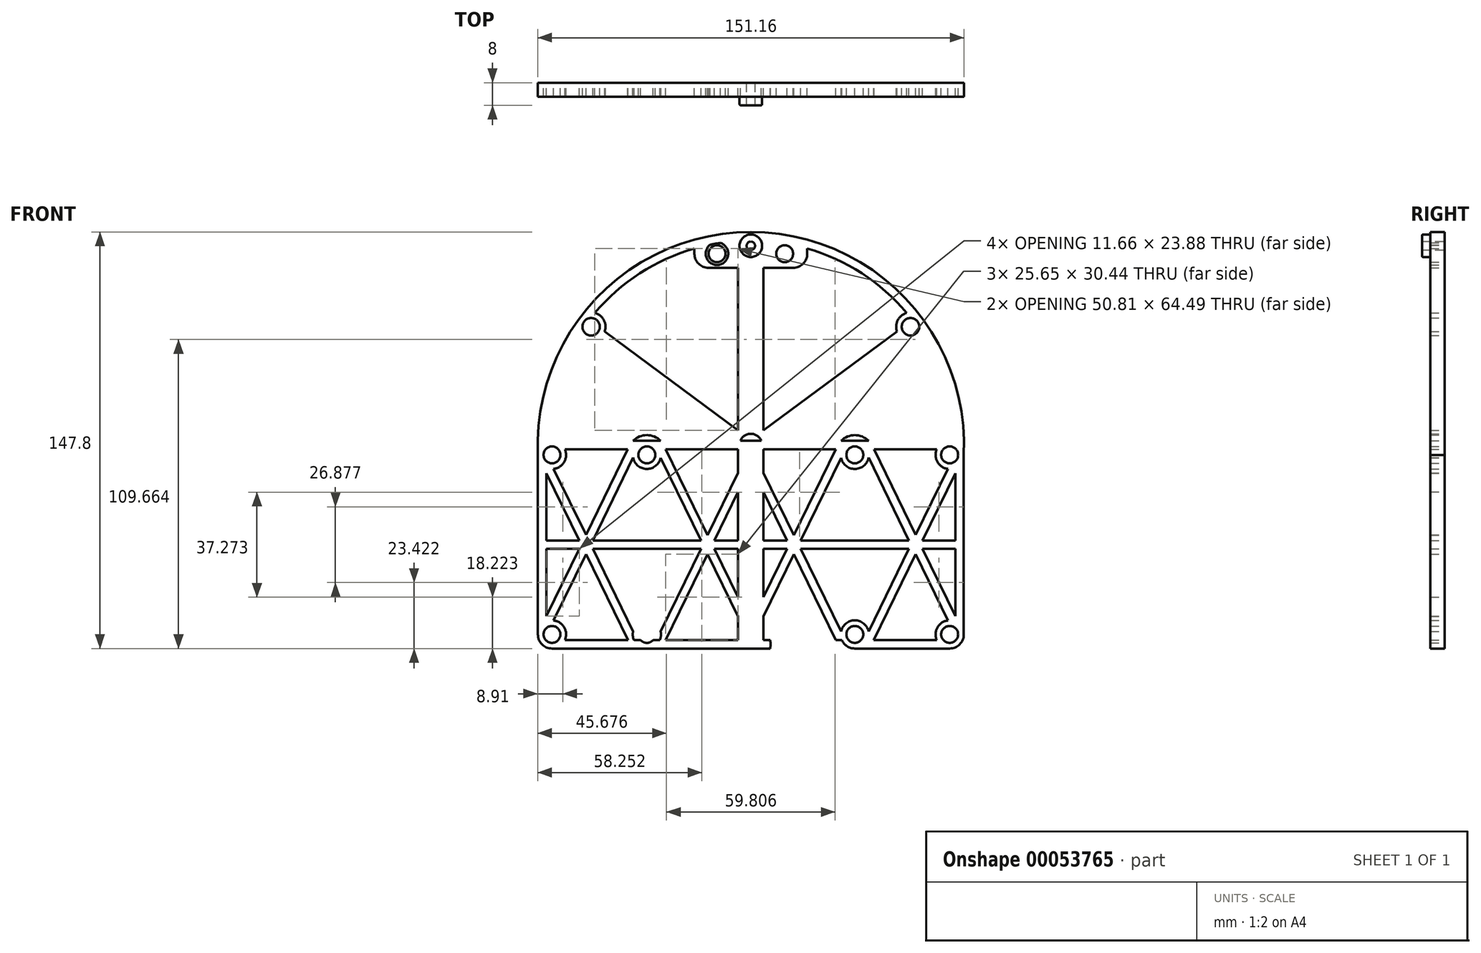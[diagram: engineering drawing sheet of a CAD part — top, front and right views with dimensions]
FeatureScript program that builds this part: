
annotation { "Feature Type Name" : "Feature", "Feature Type Description" : "" }
export const myFeature = defineFeature(function(context is Context, id is Id, definition is map)
    precondition{}
    {
        {
            var Q0;
            Q0=qCreatedBy(makeId("Front.planeOp"),FACE);
            var sketch = newSketch(context, id + "F0", { "sketchPlane" : qUnion([Q0])});
            skPoint(sketch, "E0", {"position": v(-3.58, 32.7) * mm});
            skPoint(sketch, "E1", {"position": v(-3.58, -38) * mm});
            skLineSegment(sketch, "E2.bottom", {"start": v(-8.08, 122.7) * mm, "end": v(0.92, 122.7) * mm});
            skLineSegment(sketch, "E2.top", {"start": v(-8.08, -57.3) * mm, "end": v(0.92, -57.3) * mm});
            skLineSegment(sketch, "E2.left", {"start": v(-8.08, 122.7) * mm, "end": v(-8.08, -57.3) * mm});
            skLineSegment(sketch, "E2.right", {"start": v(0.92, 122.7) * mm, "end": v(0.92, -57.3) * mm});
            skLineSegment(sketch, "E3", {"start": v(-3.58, 122.7) * mm, "end": v(-3.58, -57.3) * mm, "construction": true});
            skCircle(sketch, "E4", {"center": v(-3.58, 32.7) * mm, "radius": 1.5 * mm});
            skCircle(sketch, "E5", {"center": v(-3.58, -38) * mm, "radius": 1.5 * mm});
            skCircle(sketch, "E6", {"center": v(-3.58, 32.7) * mm, "radius": 4 * mm});
            skCircle(sketch, "E7", {"center": v(-3.58, -38) * mm, "radius": 4 * mm});
            skCircle(sketch, "E8", {"center": v(-3.58, 103.42) * mm, "radius": 1.5 * mm});
            skCircle(sketch, "E9", {"center": v(-3.58, 103.42) * mm, "radius": 4 * mm});
            skLineSegment(sketch, "E10.bottom", {"start": v(-76.08, -36.5) * mm, "end": v(68.92, -36.5) * mm});
            skLineSegment(sketch, "E10.top", {"start": v(-76.08, -39.5) * mm, "end": v(68.92, -39.5) * mm});
            skLineSegment(sketch, "E10.left", {"start": v(-76.08, -36.5) * mm, "end": v(-76.08, -39.5) * mm});
            skLineSegment(sketch, "E10.right", {"start": v(68.92, -36.5) * mm, "end": v(68.92, -39.5) * mm});
            skPoint(sketch, "E11", {"position": v(-3.58, -36.5) * mm});
            skPoint(sketch, "E12", {"position": v(-3.58, 34.2) * mm});
            skLineSegment(sketch, "E13.bottom", {"start": v(-76.08, 34.2) * mm, "end": v(68.92, 34.2) * mm});
            skLineSegment(sketch, "E13.top", {"start": v(-76.08, 31.2) * mm, "end": v(68.92, 31.2) * mm});
            skLineSegment(sketch, "E13.right", {"start": v(68.92, 34.2) * mm, "end": v(68.92, 31.2) * mm});
            skLineSegment(sketch, "E13.left", {"start": v(-76.08, 34.2) * mm, "end": v(-76.08, 31.2) * mm});
            skLineSegment(sketch, "E14.bottom", {"start": v(68.92, 34.2) * mm, "end": v(71.92, 34.2) * mm});
            skLineSegment(sketch, "E14.top", {"start": v(68.92, -39.5) * mm, "end": v(71.92, -39.5) * mm});
            skLineSegment(sketch, "E14.left", {"start": v(68.92, 34.2) * mm, "end": v(68.92, -39.5) * mm});
            skLineSegment(sketch, "E14.right", {"start": v(71.92, 34.2) * mm, "end": v(71.92, -39.5) * mm});
            skLineSegment(sketch, "E15.bottom", {"start": v(-76.08, 34.2) * mm, "end": v(-79.08, 34.2) * mm});
            skLineSegment(sketch, "E15.top", {"start": v(-76.08, -39.5) * mm, "end": v(-79.08, -39.5) * mm});
            skLineSegment(sketch, "E15.left", {"start": v(-76.08, 34.2) * mm, "end": v(-76.08, -39.5) * mm});
            skLineSegment(sketch, "E15.right", {"start": v(-79.08, 34.2) * mm, "end": v(-79.08, -39.5) * mm});
            skLineSegment(sketch, "E16", {"start": v(66.92, 34.2) * mm, "end": v(66.92, 29.2) * mm, "construction": true});
            skLineSegment(sketch, "E17", {"start": v(66.92, -39.5) * mm, "end": v(66.92, -34.5) * mm, "construction": true});
            skLineSegment(sketch, "E18", {"start": v(-74.08, 34.2) * mm, "end": v(-74.08, 29.2) * mm, "construction": true});
            skLineSegment(sketch, "E19", {"start": v(-74.08, -39.5) * mm, "end": v(-74.08, -34.5) * mm, "construction": true});
            skCircle(sketch, "E20", {"center": v(-3.58, -38) * mm, "radius": 64 * mm, "construction": true});
            skCircle(sketch, "E21", {"center": v(-3.58, 32.7) * mm, "radius": 64 * mm, "construction": true});
            skCircle(sketch, "E22", {"center": v(66.92, 29.2) * mm, "radius": 5 * mm});
            skCircle(sketch, "E23", {"center": v(66.92, -34.5) * mm, "radius": 5 * mm});
            skCircle(sketch, "E24", {"center": v(-74.08, -34.5) * mm, "radius": 5 * mm});
            skCircle(sketch, "E25", {"center": v(-74.08, 29.2) * mm, "radius": 5 * mm});
            skCircle(sketch, "E26", {"center": v(66.92, -34.5) * mm, "radius": 3 * mm});
            skCircle(sketch, "E27", {"center": v(66.92, 29.2) * mm, "radius": 3 * mm});
            skCircle(sketch, "E28", {"center": v(-74.08, 29.2) * mm, "radius": 3 * mm});
            skCircle(sketch, "E29", {"center": v(-74.08, -34.5) * mm, "radius": 3 * mm});
            skLineSegment(sketch, "E30", {"start": v(33.28, 34.2) * mm, "end": v(33.28, 29.2) * mm, "construction": true});
            skCircle(sketch, "E31", {"center": v(33.28, 29.2) * mm, "radius": 5 * mm});
            skCircle(sketch, "E32", {"center": v(33.28, 29.2) * mm, "radius": 3 * mm});
            skCircle(sketch, "E33.0.1.0", {"center": v(33.28, -34.5) * mm, "radius": 3 * mm});
            skCircle(sketch, "E33.0.1.1", {"center": v(33.28, -34.5) * mm, "radius": 5 * mm});
            skCircle(sketch, "E33.1.0.0", {"center": v(-40.44, 29.2) * mm, "radius": 3 * mm});
            skCircle(sketch, "E33.1.0.1", {"center": v(-40.44, 29.2) * mm, "radius": 5 * mm});
            skCircle(sketch, "E33.1.1.0", {"center": v(-40.44, -34.5) * mm, "radius": 3 * mm});
            skCircle(sketch, "E33.1.1.1", {"center": v(-40.44, -34.5) * mm, "radius": 5 * mm});
            skLineSegment(sketch, "E33.direction1", {"start": v(33.28, 29.2) * mm, "end": v(-40.44, 29.2) * mm, "construction": true});
            skLineSegment(sketch, "E33.direction2", {"start": v(33.28, 29.2) * mm, "end": v(33.28, -34.5) * mm, "construction": true});
            skArc(sketch, "E34", {"start": v(28.38, 34.2) * mm, "mid": v(33.28, 36.2) * mm, "end": v(38.18, 34.2) * mm});
            skArc(sketch, "E35", {"start": v(-45.34, 34.2) * mm, "mid": v(-40.44, 36.2) * mm, "end": v(-35.54, 34.2) * mm});
            skArc(sketch, "E36", {"start": v(38.18, -39.5) * mm, "mid": v(33.28, -41.5) * mm, "end": v(28.38, -39.5) * mm});
            skArc(sketch, "E37", {"start": v(-35.54, -39.5) * mm, "mid": v(-40.44, -41.5) * mm, "end": v(-45.34, -39.5) * mm});
            skCircle(sketch, "E38", {"center": v(-3.58, -38) * mm, "radius": 7 * mm});
            skArc(sketch, "E39", {"start": v(71.92, 29.2) * mm, "mid": v(-3.58, 108.29) * mm, "end": v(-79.08, 29.2) * mm});
            skArc(sketch, "E40", {"start": v(68.92, 33.79) * mm, "mid": v(-3.58, 105.21) * mm, "end": v(-76.08, 33.79) * mm});
            skLineSegment(sketch, "E41.bottom", {"start": v(-23.58, 105.6) * mm, "end": v(16.42, 105.6) * mm});
            skLineSegment(sketch, "E41.top", {"start": v(-23.58, 95.6) * mm, "end": v(16.42, 95.6) * mm});
            skLineSegment(sketch, "E41.left", {"start": v(-23.58, 105.6) * mm, "end": v(-23.58, 95.6) * mm});
            skLineSegment(sketch, "E41.right", {"start": v(16.42, 105.6) * mm, "end": v(16.42, 95.6) * mm});
            skPoint(sketch, "E42", {"position": v(-3.58, 108.29) * mm});
            skLineSegment(sketch, "E43", {"start": v(-23.58, 100.6) * mm, "end": v(16.42, 100.6) * mm, "construction": true});
            skCircle(sketch, "E44", {"center": v(8.42, 100.6) * mm, "radius": 3 * mm});
            skCircle(sketch, "E45.MirrorC", {"center": v(-15.58, 100.6) * mm, "radius": 3 * mm});
            skCircle(sketch, "E46", {"center": v(-15.58, 100.6) * mm, "radius": 4 * mm});
            skCircle(sketch, "E47", {"center": v(8.42, 100.6) * mm, "radius": 4 * mm});
            skLineSegment(sketch, "E48", {"start": v(-23.58, 105.6) * mm, "end": v(16.42, 105.6) * mm, "construction": true});
            skPoint(sketch, "E49", {"position": v(-18.58, 95.6) * mm});
            skArc(sketch, "E50", {"start": v(-23.58, 100.6) * mm, "mid": v(-22.12, 97.06) * mm, "end": v(-18.58, 95.6) * mm});
            skArc(sketch, "E51.MirrorCS", {"start": v(16.42, 100.6) * mm, "mid": v(14.96, 97.06) * mm, "end": v(11.42, 95.6) * mm});
            skLineSegment(sketch, "E52", {"start": v(-79.08, -2.65) * mm, "end": v(71.92, -2.65) * mm, "construction": true});
            skLineSegment(sketch, "E53", {"start": v(-61.08, -1.15) * mm, "end": v(-61.08, -4.15) * mm});
            skLineSegment(sketch, "E54", {"start": v(-76.08, 22.73) * mm, "end": v(-64.42, -1.15) * mm});
            skLineSegment(sketch, "E55", {"start": v(-73.48, 24.24) * mm, "end": v(-61.08, -1.15) * mm});
            skLineSegment(sketch, "E56", {"start": v(-64.42, -4.15) * mm, "end": v(-76.08, -28.03) * mm});
            skLineSegment(sketch, "E57", {"start": v(-73.48, -29.54) * mm, "end": v(-61.08, -4.15) * mm});
            skPoint(sketch, "E58", {"position": v(-61.08, -2.65) * mm});
            skLineSegment(sketch, "E59", {"start": v(-79.08, 34.2) * mm, "end": v(-61.08, -2.65) * mm, "construction": true});
            skLineSegment(sketch, "E60", {"start": v(-61.08, -2.65) * mm, "end": v(-79.08, -39.5) * mm, "construction": true});
            skLineSegment(sketch, "E61", {"start": v(-61.08, -4.15) * mm, "end": v(-76.08, -4.15) * mm});
            skLineSegment(sketch, "E62", {"start": v(-61.08, -1.15) * mm, "end": v(-76.08, -1.15) * mm});
            skLineSegment(sketch, "E63.MirrorCS", {"start": v(68.92, 22.73) * mm, "end": v(57.26, -1.15) * mm});
            skLineSegment(sketch, "E64.MirrorCS", {"start": v(66.32, 24.24) * mm, "end": v(53.92, -1.15) * mm});
            skLineSegment(sketch, "E65.MirrorCS", {"start": v(53.92, -1.15) * mm, "end": v(68.92, -1.15) * mm});
            skLineSegment(sketch, "E66.MirrorCS", {"start": v(53.92, -4.15) * mm, "end": v(68.92, -4.15) * mm});
            skLineSegment(sketch, "E67.MirrorCS", {"start": v(53.92, -1.15) * mm, "end": v(53.92, -4.15) * mm});
            skLineSegment(sketch, "E68.MirrorCS", {"start": v(66.32, -29.54) * mm, "end": v(53.92, -4.15) * mm});
            skLineSegment(sketch, "E69.MirrorCS", {"start": v(57.26, -4.15) * mm, "end": v(68.92, -28.03) * mm});
            skLineSegment(sketch, "E70", {"start": v(-64.3, 77.7) * mm, "end": v(-60.2, 74.67) * mm, "construction": true});
            skCircle(sketch, "E71", {"center": v(-60.2, 74.67) * mm, "radius": 5.1 * mm});
            skCircle(sketch, "E72", {"center": v(-60.2, 74.67) * mm, "radius": 3.1 * mm});
            skCircle(sketch, "E73.MirrorC", {"center": v(53.05, 74.67) * mm, "radius": 5.1 * mm});
            skCircle(sketch, "E74.MirrorC", {"center": v(53.05, 74.67) * mm, "radius": 3.1 * mm});
            skLineSegment(sketch, "E75.MirrorCS", {"start": v(57.14, 77.7) * mm, "end": v(53.05, 74.67) * mm, "construction": true});
            skLineSegment(sketch, "E76", {"start": v(-3.58, 32.7) * mm, "end": v(-64.3, 77.7) * mm, "construction": true});
            skLineSegment(sketch, "E77", {"start": v(-55.4, 72.97) * mm, "end": v(-8.08, 37.9) * mm});
            skLineSegment(sketch, "E78", {"start": v(-57.18, 70.56) * mm, "end": v(-8.12, 34.2) * mm});
            skLineSegment(sketch, "E79", {"start": v(-34.76, 57.68) * mm, "end": v(-36.54, 55.27) * mm, "construction": true});
            skPoint(sketch, "E80", {"position": v(-35.65, 56.47) * mm});
            skLineSegment(sketch, "E81", {"start": v(-3.58, 32.7) * mm, "end": v(-79.08, 32.7) * mm, "construction": true});
            skLineSegment(sketch, "E82.MirrorCS", {"start": v(48.24, 72.97) * mm, "end": v(0.92, 37.9) * mm});
            skLineSegment(sketch, "E83.MirrorCS", {"start": v(50.02, 70.56) * mm, "end": v(0.96, 34.2) * mm});
            skLineSegment(sketch, "E84", {"start": v(-8.08, 22.86) * mm, "end": v(-35.56, -33.41) * mm});
            skLineSegment(sketch, "E85", {"start": v(-8.08, 16.02) * mm, "end": v(-33.74, -36.5) * mm});
            skLineSegment(sketch, "E86", {"start": v(-33.74, 31.2) * mm, "end": v(-8.08, -21.32) * mm});
            skLineSegment(sketch, "E87", {"start": v(-35.56, 28.11) * mm, "end": v(-8.08, -28.16) * mm});
            skCircle(sketch, "E88", {"center": v(-40.44, 29.2) * mm, "radius": 7 * mm, "construction": true});
            skCircle(sketch, "E89", {"center": v(-40.44, -34.5) * mm, "radius": 7 * mm, "construction": true});
            skLineSegment(sketch, "E90", {"start": v(-64.42, -1.15) * mm, "end": v(-47.15, -36.5) * mm});
            skLineSegment(sketch, "E91", {"start": v(-64.42, -4.15) * mm, "end": v(-47.25, 31.2) * mm});
            skLineSegment(sketch, "E92", {"start": v(-61.08, -4.15) * mm, "end": v(-45.35, 28.25) * mm});
            skLineSegment(sketch, "E93", {"start": v(-61.08, -1.15) * mm, "end": v(-45.32, -33.41) * mm});
            skLineSegment(sketch, "E94", {"start": v(-61.08, -1.15) * mm, "end": v(-3.58, -1.15) * mm});
            skLineSegment(sketch, "E95", {"start": v(-61.08, -4.15) * mm, "end": v(-3.58, -4.15) * mm});
            skLineSegment(sketch, "E96.MirrorCS", {"start": v(0.92, 22.86) * mm, "end": v(28.4, -33.41) * mm});
            skLineSegment(sketch, "E97.MirrorCS", {"start": v(0.92, 16.02) * mm, "end": v(26.57, -36.5) * mm});
            skLineSegment(sketch, "E98.MirrorCS", {"start": v(53.92, -4.15) * mm, "end": v(38.2, 28.25) * mm});
            skLineSegment(sketch, "E99.MirrorCS", {"start": v(57.26, -4.15) * mm, "end": v(40.1, 31.2) * mm});
            skLineSegment(sketch, "E100.MirrorCS", {"start": v(53.92, -1.15) * mm, "end": v(38.16, -33.41) * mm});
            skLineSegment(sketch, "E101.MirrorCS", {"start": v(57.26, -1.15) * mm, "end": v(40, -36.5) * mm});
            skLineSegment(sketch, "E102.MirrorCS", {"start": v(53.92, -1.15) * mm, "end": v(-3.58, -1.15) * mm});
            skLineSegment(sketch, "E103.MirrorCS", {"start": v(53.92, -4.15) * mm, "end": v(-3.58, -4.15) * mm});
            skLineSegment(sketch, "E104.MirrorCS", {"start": v(26.57, 31.2) * mm, "end": v(0.92, -21.32) * mm});
            skLineSegment(sketch, "E105.MirrorCS", {"start": v(28.4, 28.11) * mm, "end": v(0.92, -28.16) * mm});
            skSolve(sketch);
        }
        {
            var Q0;
            {var subQ0=sQuery(id+"F0.wireOp",EDGE,"E13.bottom");var subQ1=sQuery(id+"F0.wireOp",EDGE,"E2.left");var subQ2=makeQuery(id+"F0.imprint","INTERSECT",VERTEX,{"derivedFrom":[subQ1,subQ0]});Q0=makeQuery(id+"F0.imprint","IMPRINT",FACE,{"disambiguationData":[TD([[makeQuery(id+"F0.imprint","IMPRINT",EDGE,{"disambiguationData":[TD([[subQ2,-1.0]])],"derivedFrom":subQ1}),-1.0]])]});}
            var Q1;
            {var subQ0=sQuery(id+"F0.wireOp",EDGE,"E13.bottom");var subQ1=sQuery(id+"F0.wireOp",EDGE,"E2.right");var subQ2=makeQuery(id+"F0.imprint","INTERSECT",VERTEX,{"derivedFrom":[subQ1,subQ0]});Q1=makeQuery(id+"F0.imprint","IMPRINT",FACE,{"disambiguationData":[TD([[makeQuery(id+"F0.imprint","IMPRINT",EDGE,{"disambiguationData":[TD([[subQ2,-1.0]])],"derivedFrom":subQ1}),1.0]])]});}
            var Q2;
            {var subQ0=sQuery(id+"F0.wireOp",EDGE,"E13.bottom");var subQ1=sQuery(id+"F0.wireOp",EDGE,"E2.right");var subQ2=makeQuery(id+"F0.imprint","INTERSECT",VERTEX,{"derivedFrom":[subQ1,subQ0]});Q2=makeQuery(id+"F0.imprint","IMPRINT",FACE,{"disambiguationData":[TD([[makeQuery(id+"F0.imprint","IMPRINT",EDGE,{"disambiguationData":[TD([[subQ2,-1.0]])],"derivedFrom":subQ1}),-1.0]])]});}
            var Q3;
            {var subQ0=sQuery(id+"F0.wireOp",EDGE,"E13.bottom");var subQ1=sQuery(id+"F0.wireOp",EDGE,"E2.left");var subQ2=makeQuery(id+"F0.imprint","INTERSECT",VERTEX,{"derivedFrom":[subQ1,subQ0]});Q3=makeQuery(id+"F0.imprint","IMPRINT",FACE,{"disambiguationData":[TD([[makeQuery(id+"F0.imprint","IMPRINT",EDGE,{"disambiguationData":[TD([[subQ2,-1.0]])],"derivedFrom":subQ1}),1.0]])]});}
            var Q4;
            {var subQ0=sQuery(id+"F0.wireOp",EDGE,"E13.top");var subQ8=sQuery(id+"F0.wireOp",EDGE,"E2.left");var subQ13=makeQuery(id+"F0.imprint","INTERSECT",VERTEX,{"derivedFrom":[subQ8,subQ0]});Q4=makeQuery(id+"F0.imprint","IMPRINT",FACE,{"disambiguationData":[TD([[makeQuery(id+"F0.imprint","IMPRINT",EDGE,{"disambiguationData":[TD([[subQ13,-1.0]])],"derivedFrom":subQ8}),1.0]])]});}
            var Q5;
            {var subQ4=sQuery(id+"F0.wireOp",EDGE,"E13.top");var subQ6=sQuery(id+"F0.wireOp",EDGE,"E28");var subQ8=makeQuery(id+"F0.imprint","INTERSECT",VERTEX,{"derivedFrom":[subQ4,subQ6]});Q5=makeQuery(id+"F0.imprint","IMPRINT",FACE,{"disambiguationData":[TD([[makeQuery(id+"F0.imprint","IMPRINT",EDGE,{"disambiguationData":[TD([[subQ8,-1.0]])],"derivedFrom":subQ4}),1.0]])]});}
            var Q6;
            {var subQ0=sQuery(id+"F0.wireOp",EDGE,"E28");var subQ1=sQuery(id+"F0.wireOp",EDGE,"E13.top");var subQ2=makeQuery(id+"F0.imprint","INTERSECT",VERTEX,{"derivedFrom":[subQ1,subQ0]});Q6=makeQuery(id+"F0.imprint","IMPRINT",FACE,{"disambiguationData":[TD([[makeQuery(id+"F0.imprint","IMPRINT",EDGE,{"disambiguationData":[TD([[subQ2,-1.0]])],"derivedFrom":subQ1}),-1.0]])]});}
            var Q7;
            {var subQ0=sQuery(id+"F0.wireOp",EDGE,"E25");var subQ2=sQuery(id+"F0.wireOp",EDGE,"E15.left");var subQ3=makeQuery(id+"F0.imprint","INTERSECT",VERTEX,{"disambiguationData":[OD(0.0)],"derivedFrom":[subQ2,subQ0]});Q7=makeQuery(id+"F0.imprint","IMPRINT",FACE,{"disambiguationData":[TD([[makeQuery(id+"F0.imprint","IMPRINT",EDGE,{"disambiguationData":[TD([[subQ3,-1.0]])],"derivedFrom":subQ2}),-1.0]])]});}
            var Q8;
            {var subQ0=sQuery(id+"F0.wireOp",EDGE,"E25");var subQ1=sQuery(id+"F0.wireOp",EDGE,"E15.left");var subQ2=makeQuery(id+"F0.imprint","INTERSECT",VERTEX,{"disambiguationData":[OD(1.0)],"derivedFrom":[subQ1,subQ0]});Q8=makeQuery(id+"F0.imprint","IMPRINT",FACE,{"disambiguationData":[TD([[makeQuery(id+"F0.imprint","IMPRINT",EDGE,{"disambiguationData":[TD([[subQ2,-1.0]])],"derivedFrom":subQ1}),-1.0]])]});}
            var Q9;
            {var subQ0=sQuery(id+"F0.wireOp",EDGE,"E24");var subQ2=sQuery(id+"F0.wireOp",EDGE,"E15.left");var subQ7=makeQuery(id+"F0.imprint","INTERSECT",VERTEX,{"disambiguationData":[OD(0.0)],"derivedFrom":[subQ2,subQ0]});Q9=makeQuery(id+"F0.imprint","IMPRINT",FACE,{"disambiguationData":[TD([[makeQuery(id+"F0.imprint","IMPRINT",EDGE,{"disambiguationData":[TD([[subQ7,-1.0]])],"derivedFrom":subQ2}),-1.0]])]});}
            var Q10;
            {var subQ2=sQuery(id+"F0.wireOp",EDGE,"E10.bottom");var subQ4=sQuery(id+"F0.wireOp",EDGE,"E29");var subQ8=makeQuery(id+"F0.imprint","INTERSECT",VERTEX,{"derivedFrom":[subQ2,subQ4]});Q10=makeQuery(id+"F0.imprint","IMPRINT",FACE,{"disambiguationData":[TD([[makeQuery(id+"F0.imprint","IMPRINT",EDGE,{"disambiguationData":[TD([[subQ8,-1.0]])],"derivedFrom":subQ2}),-1.0]])]});}
            var Q11;
            {var subQ0=sQuery(id+"F0.wireOp",EDGE,"E29");var subQ1=sQuery(id+"F0.wireOp",EDGE,"E10.bottom");var subQ2=makeQuery(id+"F0.imprint","INTERSECT",VERTEX,{"derivedFrom":[subQ1,subQ0]});Q11=makeQuery(id+"F0.imprint","IMPRINT",FACE,{"disambiguationData":[TD([[makeQuery(id+"F0.imprint","IMPRINT",EDGE,{"disambiguationData":[TD([[subQ2,-1.0]])],"derivedFrom":subQ1}),1.0]])]});}
            var Q12;
            {var subQ0=sQuery(id+"F0.wireOp",EDGE,"E23");var subQ2=sQuery(id+"F0.wireOp",EDGE,"E10.bottom");var subQ3=makeQuery(id+"F0.imprint","INTERSECT",VERTEX,{"derivedFrom":[subQ2,subQ0]});Q12=makeQuery(id+"F0.imprint","IMPRINT",FACE,{"disambiguationData":[TD([[makeQuery(id+"F0.imprint","IMPRINT",EDGE,{"disambiguationData":[TD([[subQ3,-1.0]])],"derivedFrom":subQ2}),-1.0]])]});}
            var Q13;
            {var subQ0=sQuery(id+"F0.wireOp",EDGE,"E23");var subQ2=sQuery(id+"F0.wireOp",EDGE,"E14.left");var subQ6=makeQuery(id+"F0.imprint","INTERSECT",VERTEX,{"disambiguationData":[OD(0.0)],"derivedFrom":[subQ2,subQ0]});Q13=makeQuery(id+"F0.imprint","IMPRINT",FACE,{"disambiguationData":[TD([[makeQuery(id+"F0.imprint","IMPRINT",EDGE,{"disambiguationData":[TD([[subQ6,-1.0]])],"derivedFrom":subQ2}),1.0]])]});}
            var Q14;
            {var subQ0=sQuery(id+"F0.wireOp",EDGE,"E23");var subQ1=sQuery(id+"F0.wireOp",EDGE,"E10.bottom");var subQ2=makeQuery(id+"F0.imprint","INTERSECT",VERTEX,{"derivedFrom":[subQ1,subQ0]});Q14=makeQuery(id+"F0.imprint","IMPRINT",FACE,{"disambiguationData":[TD([[makeQuery(id+"F0.imprint","IMPRINT",EDGE,{"disambiguationData":[TD([[subQ2,-1.0]])],"derivedFrom":subQ1}),1.0]])]});}
            var Q15;
            {var subQ0=sQuery(id+"F0.wireOp",EDGE,"E22");var subQ1=sQuery(id+"F0.wireOp",EDGE,"E14.left");var subQ2=makeQuery(id+"F0.imprint","INTERSECT",VERTEX,{"disambiguationData":[OD(1.0)],"derivedFrom":[subQ1,subQ0]});Q15=makeQuery(id+"F0.imprint","IMPRINT",FACE,{"disambiguationData":[TD([[makeQuery(id+"F0.imprint","IMPRINT",EDGE,{"disambiguationData":[TD([[subQ2,-1.0]])],"derivedFrom":subQ1}),1.0]])]});}
            var Q16;
            {var subQ0=sQuery(id+"F0.wireOp",EDGE,"E22");var subQ2=sQuery(id+"F0.wireOp",EDGE,"E14.left");var subQ3=makeQuery(id+"F0.imprint","INTERSECT",VERTEX,{"disambiguationData":[OD(0.0)],"derivedFrom":[subQ2,subQ0]});Q16=makeQuery(id+"F0.imprint","IMPRINT",FACE,{"disambiguationData":[TD([[makeQuery(id+"F0.imprint","IMPRINT",EDGE,{"disambiguationData":[TD([[subQ3,-1.0]])],"derivedFrom":subQ2}),1.0]])]});}
            var Q17;
            {var subQ0=sQuery(id+"F0.wireOp",EDGE,"E22");var subQ1=sQuery(id+"F0.wireOp",EDGE,"E13.top");var subQ2=makeQuery(id+"F0.imprint","INTERSECT",VERTEX,{"derivedFrom":[subQ1,subQ0]});Q17=makeQuery(id+"F0.imprint","IMPRINT",FACE,{"disambiguationData":[TD([[makeQuery(id+"F0.imprint","IMPRINT",EDGE,{"disambiguationData":[TD([[subQ2,-1.0]])],"derivedFrom":subQ1}),-1.0]])]});}
            var Q18;
            {var subQ0=sQuery(id+"F0.wireOp",EDGE,"E22");var subQ4=sQuery(id+"F0.wireOp",EDGE,"E13.top");var subQ5=makeQuery(id+"F0.imprint","INTERSECT",VERTEX,{"derivedFrom":[subQ4,subQ0]});Q18=makeQuery(id+"F0.imprint","IMPRINT",FACE,{"disambiguationData":[TD([[makeQuery(id+"F0.imprint","IMPRINT",EDGE,{"disambiguationData":[TD([[subQ5,-1.0]])],"derivedFrom":subQ4}),1.0]])]});}
            var Q19;
            {var subQ0=sQuery(id+"F0.wireOp",EDGE,"E31");var subQ1=sQuery(id+"F0.wireOp",EDGE,"E13.bottom");var subQ2=makeQuery(id+"F0.imprint","INTERSECT",VERTEX,{"derivedFrom":[subQ1,subQ0]});Q19=makeQuery(id+"F0.imprint","IMPRINT",FACE,{"disambiguationData":[TD([[makeQuery(id+"F0.imprint","IMPRINT",EDGE,{"disambiguationData":[TD([[subQ2,-1.0]])],"derivedFrom":subQ1}),-1.0]])]});}
            var Q20;
            {var subQ0=sQuery(id+"F0.wireOp",EDGE,"E31");var subQ2=sQuery(id+"F0.wireOp",EDGE,"E13.top");var subQ3=makeQuery(id+"F0.imprint","INTERSECT",VERTEX,{"disambiguationData":[OD(0.0)],"derivedFrom":[subQ2,subQ0]});Q20=makeQuery(id+"F0.imprint","IMPRINT",FACE,{"disambiguationData":[TD([[makeQuery(id+"F0.imprint","IMPRINT",EDGE,{"disambiguationData":[TD([[subQ3,-1.0]])],"derivedFrom":subQ2}),1.0]])]});}
            var Q21;
            {var subQ0=sQuery(id+"F0.wireOp",EDGE,"E31");var subQ1=sQuery(id+"F0.wireOp",EDGE,"E13.top");var subQ2=makeQuery(id+"F0.imprint","INTERSECT",VERTEX,{"disambiguationData":[OD(0.0)],"derivedFrom":[subQ1,subQ0]});Q21=makeQuery(id+"F0.imprint","IMPRINT",FACE,{"disambiguationData":[TD([[makeQuery(id+"F0.imprint","IMPRINT",EDGE,{"disambiguationData":[TD([[subQ2,-1.0]])],"derivedFrom":subQ1}),-1.0]])]});}
            var Q22;
            {var subQ0=sQuery(id+"F0.wireOp",EDGE,"E25");var subQ1=sQuery(id+"F0.wireOp",EDGE,"E13.bottom");var subQ2=makeQuery(id+"F0.imprint","INTERSECT",VERTEX,{"derivedFrom":[subQ1,subQ0]});Q22=makeQuery(id+"F0.imprint","IMPRINT",FACE,{"disambiguationData":[TD([[makeQuery(id+"F0.imprint","IMPRINT",EDGE,{"disambiguationData":[TD([[subQ2,-1.0]])],"derivedFrom":subQ1}),-1.0]])]});}
            var Q23;
            {var subQ1=sQuery(id+"F0.wireOp",EDGE,"E13.top");var subQ4=sQuery(id+"F0.wireOp",EDGE,"E33.1.0.1");var subQ7=makeQuery(id+"F0.imprint","INTERSECT",VERTEX,{"disambiguationData":[OD(0.0)],"derivedFrom":[subQ1,subQ4]});Q23=makeQuery(id+"F0.imprint","IMPRINT",FACE,{"disambiguationData":[TD([[makeQuery(id+"F0.imprint","IMPRINT",EDGE,{"disambiguationData":[TD([[subQ7,-1.0]])],"derivedFrom":subQ1}),1.0]])]});}
            var Q24;
            {var subQ0=sQuery(id+"F0.wireOp",EDGE,"E33.1.0.1");var subQ1=sQuery(id+"F0.wireOp",EDGE,"E13.top");var subQ2=makeQuery(id+"F0.imprint","INTERSECT",VERTEX,{"disambiguationData":[OD(0.0)],"derivedFrom":[subQ1,subQ0]});Q24=makeQuery(id+"F0.imprint","IMPRINT",FACE,{"disambiguationData":[TD([[makeQuery(id+"F0.imprint","IMPRINT",EDGE,{"disambiguationData":[TD([[subQ2,-1.0]])],"derivedFrom":subQ1}),-1.0]])]});}
            var Q25;
            {var subQ0=sQuery(id+"F0.wireOp",EDGE,"E33.0.1.1");var subQ1=sQuery(id+"F0.wireOp",EDGE,"E10.bottom");var subQ2=makeQuery(id+"F0.imprint","INTERSECT",VERTEX,{"disambiguationData":[OD(1.0)],"derivedFrom":[subQ1,subQ0]});Q25=makeQuery(id+"F0.imprint","IMPRINT",FACE,{"disambiguationData":[TD([[makeQuery(id+"F0.imprint","IMPRINT",EDGE,{"disambiguationData":[TD([[subQ2,-1.0]])],"derivedFrom":subQ1}),-1.0]])]});}
            var Q26;
            {var subQ1=sQuery(id+"F0.wireOp",EDGE,"E10.bottom");var subQ4=sQuery(id+"F0.wireOp",EDGE,"E33.0.1.1");var subQ9=makeQuery(id+"F0.imprint","INTERSECT",VERTEX,{"disambiguationData":[OD(0.0)],"derivedFrom":[subQ1,subQ4]});Q26=makeQuery(id+"F0.imprint","IMPRINT",FACE,{"disambiguationData":[TD([[makeQuery(id+"F0.imprint","IMPRINT",EDGE,{"disambiguationData":[TD([[subQ9,-1.0]])],"derivedFrom":subQ1}),-1.0]])]});}
            var Q27;
            {var subQ0=sQuery(id+"F0.wireOp",EDGE,"E33.0.1.1");var subQ1=sQuery(id+"F0.wireOp",EDGE,"E10.bottom");var subQ2=makeQuery(id+"F0.imprint","INTERSECT",VERTEX,{"disambiguationData":[OD(0.0)],"derivedFrom":[subQ1,subQ0]});Q27=makeQuery(id+"F0.imprint","IMPRINT",FACE,{"disambiguationData":[TD([[makeQuery(id+"F0.imprint","IMPRINT",EDGE,{"disambiguationData":[TD([[subQ2,-1.0]])],"derivedFrom":subQ1}),1.0]])]});}
            var Q28;
            {var subQ0=sQuery(id+"F0.wireOp",EDGE,"E24");var subQ1=sQuery(id+"F0.wireOp",EDGE,"E10.bottom");var subQ2=makeQuery(id+"F0.imprint","INTERSECT",VERTEX,{"derivedFrom":[subQ1,subQ0]});Q28=makeQuery(id+"F0.imprint","IMPRINT",FACE,{"disambiguationData":[TD([[makeQuery(id+"F0.imprint","IMPRINT",EDGE,{"disambiguationData":[TD([[subQ2,-1.0]])],"derivedFrom":subQ1}),-1.0]])]});}
            var Q29;
            {var subQ0=sQuery(id+"F0.wireOp",EDGE,"E33.1.1.1");var subQ1=sQuery(id+"F0.wireOp",EDGE,"E10.bottom");var subQ2=makeQuery(id+"F0.imprint","INTERSECT",VERTEX,{"disambiguationData":[OD(0.0)],"derivedFrom":[subQ1,subQ0]});Q29=makeQuery(id+"F0.imprint","IMPRINT",FACE,{"disambiguationData":[TD([[makeQuery(id+"F0.imprint","IMPRINT",EDGE,{"disambiguationData":[TD([[subQ2,-1.0]])],"derivedFrom":subQ1}),1.0]])]});}
            var Q30;
            {var subQ1=sQuery(id+"F0.wireOp",EDGE,"E10.bottom");var subQ4=sQuery(id+"F0.wireOp",EDGE,"E33.1.1.1");var subQ9=makeQuery(id+"F0.imprint","INTERSECT",VERTEX,{"disambiguationData":[OD(0.0)],"derivedFrom":[subQ1,subQ4]});Q30=makeQuery(id+"F0.imprint","IMPRINT",FACE,{"disambiguationData":[TD([[makeQuery(id+"F0.imprint","IMPRINT",EDGE,{"disambiguationData":[TD([[subQ9,-1.0]])],"derivedFrom":subQ1}),-1.0]])]});}
            var Q31;
            {var subQ0=sQuery(id+"F0.wireOp",EDGE,"E34");Q31=makeQuery(id+"F0.imprint","IMPRINT",FACE,{"disambiguationData":[TD([[makeQuery(id+"F0.imprint","IMPRINT",EDGE,{"derivedFrom":subQ0}),-1.0]])]});}
            var Q32;
            {var subQ0=sQuery(id+"F0.wireOp",EDGE,"E35");Q32=makeQuery(id+"F0.imprint","IMPRINT",FACE,{"disambiguationData":[TD([[makeQuery(id+"F0.imprint","IMPRINT",EDGE,{"derivedFrom":subQ0}),-1.0]])]});}
            var Q33;
            {var subQ0=sQuery(id+"F0.wireOp",EDGE,"E36");Q33=makeQuery(id+"F0.imprint","IMPRINT",FACE,{"disambiguationData":[TD([[makeQuery(id+"F0.imprint","IMPRINT",EDGE,{"derivedFrom":subQ0}),-1.0]])]});}
            var Q34;
            {var subQ0=sQuery(id+"F0.wireOp",EDGE,"E37");Q34=makeQuery(id+"F0.imprint","IMPRINT",FACE,{"disambiguationData":[TD([[makeQuery(id+"F0.imprint","IMPRINT",EDGE,{"derivedFrom":subQ0}),-1.0]])]});}
            var Q35;
            {var subQ0=sQuery(id+"F0.wireOp",EDGE,"E33.1.1.1");var subQ1=sQuery(id+"F0.wireOp",EDGE,"E10.bottom");var subQ2=makeQuery(id+"F0.imprint","INTERSECT",VERTEX,{"disambiguationData":[OD(1.0)],"derivedFrom":[subQ1,subQ0]});Q35=makeQuery(id+"F0.imprint","IMPRINT",FACE,{"disambiguationData":[TD([[makeQuery(id+"F0.imprint","IMPRINT",EDGE,{"disambiguationData":[TD([[subQ2,-1.0]])],"derivedFrom":subQ1}),-1.0]])]});}
            var Q36;
            {var subQ1=sQuery(id+"F0.wireOp",EDGE,"E10.bottom");var subQ6=sQuery(id+"F0.wireOp",EDGE,"E38");var subQ8=makeQuery(id+"F0.imprint","INTERSECT",VERTEX,{"disambiguationData":[OD(1.0)],"derivedFrom":[subQ1,subQ6]});Q36=makeQuery(id+"F0.imprint","IMPRINT",FACE,{"disambiguationData":[TD([[makeQuery(id+"F0.imprint","IMPRINT",EDGE,{"disambiguationData":[TD([[subQ8,-1.0]])],"derivedFrom":subQ1}),-1.0]])]});}
            var Q37;
            {var subQ0=sQuery(id+"F0.wireOp",EDGE,"E14.bottom");Q37=makeQuery(id+"F0.imprint","IMPRINT",FACE,{"disambiguationData":[TD([[makeQuery(id+"F0.imprint","IMPRINT",EDGE,{"derivedFrom":subQ0}),1.0]])]});}
            var Q38;
            {var subQ1=sQuery(id+"F0.wireOp",EDGE,"E15.bottom");Q38=makeQuery(id+"F0.imprint","IMPRINT",FACE,{"disambiguationData":[TD([[makeQuery(id+"F0.imprint","IMPRINT",EDGE,{"derivedFrom":subQ1}),-1.0]])]});}
            var Q39;
            {var subQ0=sQuery(id+"F0.wireOp",EDGE,"E39");var subQ1=sQuery(id+"F0.wireOp",EDGE,"E2.left");var subQ2=makeQuery(id+"F0.imprint","INTERSECT",VERTEX,{"derivedFrom":[subQ1,subQ0]});Q39=makeQuery(id+"F0.imprint","IMPRINT",FACE,{"disambiguationData":[TD([[makeQuery(id+"F0.imprint","IMPRINT",EDGE,{"disambiguationData":[TD([[subQ2,-1.0]])],"derivedFrom":subQ1}),1.0]])]});}
            var Q40;
            {var subQ0=sQuery(id+"F0.wireOp",EDGE,"E14.bottom");Q40=makeQuery(id+"F0.imprint","IMPRINT",FACE,{"disambiguationData":[TD([[makeQuery(id+"F0.imprint","IMPRINT",EDGE,{"derivedFrom":subQ0}),-1.0]])]});}
            var Q41;
            {var subQ4=sQuery(id+"F0.wireOp",EDGE,"E40");var subQ11=sQuery(id+"F0.wireOp",EDGE,"E2.left");var subQ12=makeQuery(id+"F0.imprint","INTERSECT",VERTEX,{"derivedFrom":[subQ11,subQ4]});Q41=makeQuery(id+"F0.imprint","IMPRINT",FACE,{"disambiguationData":[TD([[makeQuery(id+"F0.imprint","IMPRINT",EDGE,{"disambiguationData":[TD([[subQ12,-1.0]])],"derivedFrom":subQ11}),1.0]])]});}
            var Q42;
            {var subQ0=sQuery(id+"F0.wireOp",EDGE,"E15.bottom");Q42=makeQuery(id+"F0.imprint","IMPRINT",FACE,{"disambiguationData":[TD([[makeQuery(id+"F0.imprint","IMPRINT",EDGE,{"derivedFrom":subQ0}),1.0]])]});}
            var Q43;
            {var subQ0=sQuery(id+"F0.wireOp",EDGE,"E28");var subQ1=sQuery(id+"F0.wireOp",EDGE,"E15.left");var subQ2=makeQuery(id+"F0.imprint","INTERSECT",VERTEX,{"disambiguationData":[OD(1.0)],"derivedFrom":[subQ1,subQ0]});Q43=makeQuery(id+"F0.imprint","IMPRINT",FACE,{"disambiguationData":[TD([[makeQuery(id+"F0.imprint","IMPRINT",EDGE,{"disambiguationData":[TD([[subQ2,-1.0]])],"derivedFrom":subQ1}),-1.0]])]});}
            var Q44;
            {var subQ2=sQuery(id+"F0.wireOp",EDGE,"E14.left");var subQ4=sQuery(id+"F0.wireOp",EDGE,"E27");var subQ5=makeQuery(id+"F0.imprint","INTERSECT",VERTEX,{"disambiguationData":[OD(1.0)],"derivedFrom":[subQ2,subQ4]});Q44=makeQuery(id+"F0.imprint","IMPRINT",FACE,{"disambiguationData":[TD([[makeQuery(id+"F0.imprint","IMPRINT",EDGE,{"disambiguationData":[TD([[subQ5,-1.0]])],"derivedFrom":subQ2}),1.0]])]});}
            var Q45;
            {var subQ0=sQuery(id+"F0.wireOp",EDGE,"E13.bottom");var subQ1=sQuery(id+"F0.wireOp",EDGE,"E4");var subQ2=makeQuery(id+"F0.imprint","INTERSECT",VERTEX,{"derivedFrom":[subQ1,subQ0]});Q45=makeQuery(id+"F0.imprint","IMPRINT",FACE,{"disambiguationData":[TD([[makeQuery(id+"F0.imprint","IMPRINT",EDGE,{"disambiguationData":[TD([[subQ2,-1.0]])],"derivedFrom":subQ1}),-1.0]])]});}
            var Q46;
            {var subQ0=sQuery(id+"F0.wireOp",EDGE,"E13.bottom");var subQ1=sQuery(id+"F0.wireOp",EDGE,"E4");var subQ2=makeQuery(id+"F0.imprint","INTERSECT",VERTEX,{"derivedFrom":[subQ1,subQ0]});Q46=makeQuery(id+"F0.imprint","IMPRINT",FACE,{"disambiguationData":[TD([[makeQuery(id+"F0.imprint","IMPRINT",EDGE,{"disambiguationData":[TD([[subQ2,1.0]])],"derivedFrom":subQ1}),-1.0]])]});}
            var Q47;
            {var subQ0=sQuery(id+"F0.wireOp",EDGE,"E4");var subQ1=makeQuery(id+"F0.imprint","INTERSECT",VERTEX,{"derivedFrom":[subQ0,sQuery(id+"F0.wireOp",EDGE,"E13.bottom")]});Q47=makeQuery(id+"F0.imprint","IMPRINT",FACE,{"disambiguationData":[TD([[makeQuery(id+"F0.imprint","IMPRINT",EDGE,{"disambiguationData":[TD([[subQ1,-1.0]])],"derivedFrom":subQ0}),1.0]])]});}
            var Q48;
            {var subQ0=sQuery(id+"F0.wireOp",EDGE,"E13.top");var subQ1=sQuery(id+"F0.wireOp",EDGE,"E6");var subQ2=makeQuery(id+"F0.imprint","INTERSECT",VERTEX,{"disambiguationData":[OD(0.0)],"derivedFrom":[subQ1,subQ0]});Q48=makeQuery(id+"F0.imprint","IMPRINT",FACE,{"disambiguationData":[TD([[makeQuery(id+"F0.imprint","IMPRINT",EDGE,{"disambiguationData":[TD([[subQ2,-1.0]])],"derivedFrom":subQ1}),1.0]])]});}
            var Q49;
            {var subQ0=sQuery(id+"F0.wireOp",EDGE,"E13.bottom");var subQ1=sQuery(id+"F0.wireOp",EDGE,"E6");var subQ2=makeQuery(id+"F0.imprint","INTERSECT",VERTEX,{"disambiguationData":[OD(0.0)],"derivedFrom":[subQ1,subQ0]});Q49=makeQuery(id+"F0.imprint","IMPRINT",FACE,{"disambiguationData":[TD([[makeQuery(id+"F0.imprint","IMPRINT",EDGE,{"disambiguationData":[TD([[subQ2,1.0]])],"derivedFrom":subQ1}),1.0]])]});}
            var Q50;
            {var subQ0=sQuery(id+"F0.wireOp",EDGE,"E10.bottom");var subQ1=sQuery(id+"F0.wireOp",EDGE,"E2.left");var subQ2=makeQuery(id+"F0.imprint","INTERSECT",VERTEX,{"derivedFrom":[subQ1,subQ0]});Q50=makeQuery(id+"F0.imprint","IMPRINT",FACE,{"disambiguationData":[TD([[makeQuery(id+"F0.imprint","IMPRINT",EDGE,{"disambiguationData":[TD([[subQ2,-1.0]])],"derivedFrom":subQ1}),-1.0]])]});}
            var Q51;
            {var subQ0=sQuery(id+"F0.wireOp",EDGE,"E10.bottom");var subQ1=sQuery(id+"F0.wireOp",EDGE,"E5");var subQ2=makeQuery(id+"F0.imprint","INTERSECT",VERTEX,{"derivedFrom":[subQ1,subQ0]});Q51=makeQuery(id+"F0.imprint","IMPRINT",FACE,{"disambiguationData":[TD([[makeQuery(id+"F0.imprint","IMPRINT",EDGE,{"disambiguationData":[TD([[subQ2,-1.0]])],"derivedFrom":subQ1}),-1.0]])]});}
            var Q52;
            {var subQ0=sQuery(id+"F0.wireOp",EDGE,"E10.bottom");var subQ1=sQuery(id+"F0.wireOp",EDGE,"E7");var subQ2=makeQuery(id+"F0.imprint","INTERSECT",VERTEX,{"disambiguationData":[OD(0.0)],"derivedFrom":[subQ1,subQ0]});Q52=makeQuery(id+"F0.imprint","IMPRINT",FACE,{"disambiguationData":[TD([[makeQuery(id+"F0.imprint","IMPRINT",EDGE,{"disambiguationData":[TD([[subQ2,1.0]])],"derivedFrom":subQ1}),1.0]])]});}
            var Q53;
            {var subQ1=sQuery(id+"F0.wireOp",EDGE,"E2.left");var subQ5=sQuery(id+"F0.wireOp",EDGE,"E38");var subQ10=makeQuery(id+"F0.imprint","INTERSECT",VERTEX,{"disambiguationData":[OD(1.0)],"derivedFrom":[subQ1,subQ5]});Q53=makeQuery(id+"F0.imprint","IMPRINT",FACE,{"disambiguationData":[TD([[makeQuery(id+"F0.imprint","IMPRINT",EDGE,{"disambiguationData":[TD([[subQ10,-1.0]])],"derivedFrom":subQ1}),1.0]])]});}
            var Q54;
            {var subQ0=sQuery(id+"F0.wireOp",EDGE,"E5");var subQ1=makeQuery(id+"F0.imprint","INTERSECT",VERTEX,{"derivedFrom":[subQ0,sQuery(id+"F0.wireOp",EDGE,"E10.bottom")]});Q54=makeQuery(id+"F0.imprint","IMPRINT",FACE,{"disambiguationData":[TD([[makeQuery(id+"F0.imprint","IMPRINT",EDGE,{"disambiguationData":[TD([[subQ1,-1.0]])],"derivedFrom":subQ0}),1.0]])]});}
            var Q55;
            {var subQ0=sQuery(id+"F0.wireOp",EDGE,"E10.bottom");var subQ1=sQuery(id+"F0.wireOp",EDGE,"E5");var subQ2=makeQuery(id+"F0.imprint","INTERSECT",VERTEX,{"derivedFrom":[subQ1,subQ0]});Q55=makeQuery(id+"F0.imprint","IMPRINT",FACE,{"disambiguationData":[TD([[makeQuery(id+"F0.imprint","IMPRINT",EDGE,{"disambiguationData":[TD([[subQ2,1.0]])],"derivedFrom":subQ1}),-1.0]])]});}
            var Q56;
            {var subQ0=sQuery(id+"F0.wireOp",EDGE,"E10.bottom");var subQ1=sQuery(id+"F0.wireOp",EDGE,"E2.right");var subQ2=makeQuery(id+"F0.imprint","INTERSECT",VERTEX,{"derivedFrom":[subQ1,subQ0]});Q56=makeQuery(id+"F0.imprint","IMPRINT",FACE,{"disambiguationData":[TD([[makeQuery(id+"F0.imprint","IMPRINT",EDGE,{"disambiguationData":[TD([[subQ2,-1.0]])],"derivedFrom":subQ1}),1.0]])]});}
            var Q57;
            {var subQ0=sQuery(id+"F0.wireOp",EDGE,"E10.bottom");var subQ1=sQuery(id+"F0.wireOp",EDGE,"E2.right");var subQ2=makeQuery(id+"F0.imprint","INTERSECT",VERTEX,{"derivedFrom":[subQ1,subQ0]});Q57=makeQuery(id+"F0.imprint","IMPRINT",FACE,{"disambiguationData":[TD([[makeQuery(id+"F0.imprint","IMPRINT",EDGE,{"disambiguationData":[TD([[subQ2,-1.0]])],"derivedFrom":subQ1}),-1.0]])]});}
            var Q58;
            {var subQ0=sQuery(id+"F0.wireOp",EDGE,"E10.bottom");var subQ1=sQuery(id+"F0.wireOp",EDGE,"E2.left");var subQ2=makeQuery(id+"F0.imprint","INTERSECT",VERTEX,{"derivedFrom":[subQ1,subQ0]});Q58=makeQuery(id+"F0.imprint","IMPRINT",FACE,{"disambiguationData":[TD([[makeQuery(id+"F0.imprint","IMPRINT",EDGE,{"disambiguationData":[TD([[subQ2,-1.0]])],"derivedFrom":subQ1}),1.0]])]});}
            var Q59;
            {var subQ1=sQuery(id+"F0.wireOp",EDGE,"E2.left");var subQ6=sQuery(id+"F0.wireOp",EDGE,"E39");var subQ8=makeQuery(id+"F0.imprint","INTERSECT",VERTEX,{"derivedFrom":[subQ1,subQ6]});Q59=makeQuery(id+"F0.imprint","IMPRINT",FACE,{"disambiguationData":[TD([[makeQuery(id+"F0.imprint","IMPRINT",EDGE,{"disambiguationData":[TD([[subQ8,-1.0]])],"derivedFrom":subQ1}),-1.0]])]});}
            var Q60;
            {var subQ1=sQuery(id+"F0.wireOp",EDGE,"E2.right");var subQ5=sQuery(id+"F0.wireOp",EDGE,"E39");var subQ6=makeQuery(id+"F0.imprint","INTERSECT",VERTEX,{"derivedFrom":[subQ1,subQ5]});Q60=makeQuery(id+"F0.imprint","IMPRINT",FACE,{"disambiguationData":[TD([[makeQuery(id+"F0.imprint","IMPRINT",EDGE,{"disambiguationData":[TD([[subQ6,-1.0]])],"derivedFrom":subQ1}),1.0]])]});}
            var Q61;
            {var subQ3=sQuery(id+"F0.wireOp",EDGE,"E2.right");var subQ5=sQuery(id+"F0.wireOp",EDGE,"E40");var subQ6=makeQuery(id+"F0.imprint","INTERSECT",VERTEX,{"derivedFrom":[subQ3,subQ5]});Q61=makeQuery(id+"F0.imprint","IMPRINT",FACE,{"disambiguationData":[TD([[makeQuery(id+"F0.imprint","IMPRINT",EDGE,{"disambiguationData":[TD([[subQ6,-1.0]])],"derivedFrom":subQ3}),1.0]])]});}
            var Q62;
            {var subQ3=sQuery(id+"F0.wireOp",EDGE,"E2.left");var subQ5=sQuery(id+"F0.wireOp",EDGE,"E40");var subQ6=makeQuery(id+"F0.imprint","INTERSECT",VERTEX,{"derivedFrom":[subQ3,subQ5]});Q62=makeQuery(id+"F0.imprint","IMPRINT",FACE,{"disambiguationData":[TD([[makeQuery(id+"F0.imprint","IMPRINT",EDGE,{"disambiguationData":[TD([[subQ6,-1.0]])],"derivedFrom":subQ3}),-1.0]])]});}
            var Q63;
            {var subQ0=sQuery(id+"F0.wireOp",EDGE,"E41.left");var subQ1=sQuery(id+"F0.wireOp",EDGE,"E39");var subQ2=makeQuery(id+"F0.imprint","INTERSECT",VERTEX,{"derivedFrom":[subQ1,subQ0]});Q63=makeQuery(id+"F0.imprint","IMPRINT",FACE,{"disambiguationData":[TD([[makeQuery(id+"F0.imprint","IMPRINT",EDGE,{"disambiguationData":[TD([[subQ2,1.0]])],"derivedFrom":subQ1}),1.0]])]});}
            var Q64;
            {var subQ0=sQuery(id+"F0.wireOp",EDGE,"E41.right");var subQ1=sQuery(id+"F0.wireOp",EDGE,"E39");var subQ2=makeQuery(id+"F0.imprint","INTERSECT",VERTEX,{"derivedFrom":[subQ1,subQ0]});Q64=makeQuery(id+"F0.imprint","IMPRINT",FACE,{"disambiguationData":[TD([[makeQuery(id+"F0.imprint","IMPRINT",EDGE,{"disambiguationData":[TD([[subQ2,-1.0]])],"derivedFrom":subQ1}),1.0]])]});}
            var Q65;
            {var subQ4=sQuery(id+"F0.wireOp",EDGE,"E2.left");var subQ6=sQuery(id+"F0.wireOp",EDGE,"E41.top");var subQ10=makeQuery(id+"F0.imprint","INTERSECT",VERTEX,{"derivedFrom":[subQ4,subQ6]});Q65=makeQuery(id+"F0.imprint","IMPRINT",FACE,{"disambiguationData":[TD([[makeQuery(id+"F0.imprint","IMPRINT",EDGE,{"disambiguationData":[TD([[subQ10,-1.0]])],"derivedFrom":subQ4}),1.0]])]});}
            var Q66;
            {var subQ1=sQuery(id+"F0.wireOp",EDGE,"E2.right");var subQ6=sQuery(id+"F0.wireOp",EDGE,"E41.bottom");var subQ8=makeQuery(id+"F0.imprint","INTERSECT",VERTEX,{"derivedFrom":[subQ1,subQ6]});Q66=makeQuery(id+"F0.imprint","IMPRINT",FACE,{"disambiguationData":[TD([[makeQuery(id+"F0.imprint","IMPRINT",EDGE,{"disambiguationData":[TD([[subQ8,-1.0]])],"derivedFrom":subQ1}),1.0]])]});}
            var Q67;
            {var subQ1=sQuery(id+"F0.wireOp",EDGE,"E41.bottom");var subQ3=sQuery(id+"F0.wireOp",EDGE,"E2.left");var subQ4=makeQuery(id+"F0.imprint","INTERSECT",VERTEX,{"derivedFrom":[subQ3,subQ1]});Q67=makeQuery(id+"F0.imprint","IMPRINT",FACE,{"disambiguationData":[TD([[makeQuery(id+"F0.imprint","IMPRINT",EDGE,{"disambiguationData":[TD([[subQ4,-1.0]])],"derivedFrom":subQ3}),-1.0]])]});}
            var Q68;
            {var subQ0=sQuery(id+"F0.wireOp",EDGE,"E41.bottom");var subQ1=sQuery(id+"F0.wireOp",EDGE,"E2.left");var subQ2=makeQuery(id+"F0.imprint","INTERSECT",VERTEX,{"derivedFrom":[subQ1,subQ0]});Q68=makeQuery(id+"F0.imprint","IMPRINT",FACE,{"disambiguationData":[TD([[makeQuery(id+"F0.imprint","IMPRINT",EDGE,{"disambiguationData":[TD([[subQ2,-1.0]])],"derivedFrom":subQ1}),1.0]])]});}
            var Q69;
            {var subQ0=sQuery(id+"F0.wireOp",EDGE,"E41.bottom");var subQ1=sQuery(id+"F0.wireOp",EDGE,"E2.right");var subQ2=makeQuery(id+"F0.imprint","INTERSECT",VERTEX,{"derivedFrom":[subQ1,subQ0]});Q69=makeQuery(id+"F0.imprint","IMPRINT",FACE,{"disambiguationData":[TD([[makeQuery(id+"F0.imprint","IMPRINT",EDGE,{"disambiguationData":[TD([[subQ2,-1.0]])],"derivedFrom":subQ1}),-1.0]])]});}
            var Q70;
            Q70=makeQuery(id+"F0.imprint","IMPRINT",FACE,{"disambiguationData":[TD([[makeQuery(id+"F0.imprint","IMPRINT",EDGE,{"derivedFrom":sQuery(id+"F0.wireOp",EDGE,"E44")}),-1.0]])]});
            var Q71;
            Q71=makeQuery(id+"F0.imprint","IMPRINT",FACE,{"disambiguationData":[TD([[makeQuery(id+"F0.imprint","IMPRINT",EDGE,{"derivedFrom":sQuery(id+"F0.wireOp",EDGE,"E45.MirrorC")}),1.0]])]});
            var Q72;
            {var subQ0=sQuery(id+"F0.wireOp",EDGE,"E46");var subQ1=sQuery(id+"F0.wireOp",EDGE,"E40");var subQ2=makeQuery(id+"F0.imprint","INTERSECT",VERTEX,{"disambiguationData":[OD(0.0)],"derivedFrom":[subQ1,subQ0]});Q72=makeQuery(id+"F0.imprint","IMPRINT",FACE,{"disambiguationData":[TD([[makeQuery(id+"F0.imprint","IMPRINT",EDGE,{"disambiguationData":[TD([[subQ2,-1.0]])],"derivedFrom":subQ1}),-1.0]])]});}
            var Q73;
            {var subQ0=sQuery(id+"F0.wireOp",EDGE,"E47");var subQ1=sQuery(id+"F0.wireOp",EDGE,"E40");var subQ2=makeQuery(id+"F0.imprint","INTERSECT",VERTEX,{"disambiguationData":[OD(0.0)],"derivedFrom":[subQ1,subQ0]});Q73=makeQuery(id+"F0.imprint","IMPRINT",FACE,{"disambiguationData":[TD([[makeQuery(id+"F0.imprint","IMPRINT",EDGE,{"disambiguationData":[TD([[subQ2,-1.0]])],"derivedFrom":subQ1}),-1.0]])]});}
            var Q74;
            {var subQ1=sQuery(id+"F0.wireOp",EDGE,"E54");Q74=makeQuery(id+"F0.imprint","IMPRINT",FACE,{"disambiguationData":[TD([[makeQuery(id+"F0.imprint","IMPRINT",EDGE,{"derivedFrom":subQ1}),1.0]])]});}
            var Q75;
            {var subQ0=sQuery(id+"F0.wireOp",EDGE,"E53");Q75=makeQuery(id+"F0.imprint","IMPRINT",FACE,{"disambiguationData":[TD([[makeQuery(id+"F0.imprint","IMPRINT",EDGE,{"derivedFrom":subQ0}),-1.0]])]});}
            var Q76;
            {var subQ1=sQuery(id+"F0.wireOp",EDGE,"E56");Q76=makeQuery(id+"F0.imprint","IMPRINT",FACE,{"disambiguationData":[TD([[makeQuery(id+"F0.imprint","IMPRINT",EDGE,{"derivedFrom":subQ1}),1.0]])]});}
            var Q77;
            {var subQ1=sQuery(id+"F0.wireOp",EDGE,"E63.MirrorCS");Q77=makeQuery(id+"F0.imprint","IMPRINT",FACE,{"disambiguationData":[TD([[makeQuery(id+"F0.imprint","IMPRINT",EDGE,{"derivedFrom":subQ1}),-1.0]])]});}
            var Q78;
            {var subQ0=sQuery(id+"F0.wireOp",EDGE,"E67.MirrorCS");Q78=makeQuery(id+"F0.imprint","IMPRINT",FACE,{"disambiguationData":[TD([[makeQuery(id+"F0.imprint","IMPRINT",EDGE,{"derivedFrom":subQ0}),1.0]])]});}
            var Q79;
            {var subQ0=sQuery(id+"F0.wireOp",EDGE,"E68.MirrorCS");Q79=makeQuery(id+"F0.imprint","IMPRINT",FACE,{"disambiguationData":[TD([[makeQuery(id+"F0.imprint","IMPRINT",EDGE,{"derivedFrom":subQ0}),-1.0]])]});}
            var Q80;
            {var subQ0=sQuery(id+"F0.wireOp",EDGE,"E41.left");var subQ5=sQuery(id+"F0.wireOp",EDGE,"E40");var subQ6=makeQuery(id+"F0.imprint","INTERSECT",VERTEX,{"derivedFrom":[subQ5,subQ0]});Q80=makeQuery(id+"F0.imprint","IMPRINT",FACE,{"disambiguationData":[TD([[makeQuery(id+"F0.imprint","IMPRINT",EDGE,{"disambiguationData":[TD([[subQ6,-1.0]])],"derivedFrom":subQ5}),-1.0]])]});}
            var Q81;
            {var subQ0=sQuery(id+"F0.wireOp",EDGE,"E71");var subQ2=sQuery(id+"F0.wireOp",EDGE,"E40");var subQ6=makeQuery(id+"F0.imprint","INTERSECT",VERTEX,{"disambiguationData":[OD(0.0)],"derivedFrom":[subQ2,subQ0]});Q81=makeQuery(id+"F0.imprint","IMPRINT",FACE,{"disambiguationData":[TD([[makeQuery(id+"F0.imprint","IMPRINT",EDGE,{"disambiguationData":[TD([[subQ6,-1.0]])],"derivedFrom":subQ2}),-1.0]])]});}
            var Q82;
            {var subQ0=sQuery(id+"F0.wireOp",EDGE,"E71");var subQ1=sQuery(id+"F0.wireOp",EDGE,"E40");var subQ2=makeQuery(id+"F0.imprint","INTERSECT",VERTEX,{"disambiguationData":[OD(0.0)],"derivedFrom":[subQ1,subQ0]});Q82=makeQuery(id+"F0.imprint","IMPRINT",FACE,{"disambiguationData":[TD([[makeQuery(id+"F0.imprint","IMPRINT",EDGE,{"disambiguationData":[TD([[subQ2,-1.0]])],"derivedFrom":subQ1}),1.0]])]});}
            var Q83;
            {var subQ3=sQuery(id+"F0.wireOp",EDGE,"E73.MirrorC");var subQ5=sQuery(id+"F0.wireOp",EDGE,"E40");var subQ6=makeQuery(id+"F0.imprint","INTERSECT",VERTEX,{"disambiguationData":[OD(1.0)],"derivedFrom":[subQ5,subQ3]});Q83=makeQuery(id+"F0.imprint","IMPRINT",FACE,{"disambiguationData":[TD([[makeQuery(id+"F0.imprint","IMPRINT",EDGE,{"disambiguationData":[TD([[subQ6,-1.0]])],"derivedFrom":subQ5}),-1.0]])]});}
            var Q84;
            {var subQ1=sQuery(id+"F0.wireOp",EDGE,"E40");var subQ3=sQuery(id+"F0.wireOp",EDGE,"E73.MirrorC");var subQ6=makeQuery(id+"F0.imprint","INTERSECT",VERTEX,{"disambiguationData":[OD(0.0)],"derivedFrom":[subQ1,subQ3]});Q84=makeQuery(id+"F0.imprint","IMPRINT",FACE,{"disambiguationData":[TD([[makeQuery(id+"F0.imprint","IMPRINT",EDGE,{"disambiguationData":[TD([[subQ6,-1.0]])],"derivedFrom":subQ1}),-1.0]])]});}
            var Q85;
            {var subQ0=sQuery(id+"F0.wireOp",EDGE,"E73.MirrorC");var subQ1=sQuery(id+"F0.wireOp",EDGE,"E40");var subQ2=makeQuery(id+"F0.imprint","INTERSECT",VERTEX,{"disambiguationData":[OD(0.0)],"derivedFrom":[subQ1,subQ0]});Q85=makeQuery(id+"F0.imprint","IMPRINT",FACE,{"disambiguationData":[TD([[makeQuery(id+"F0.imprint","IMPRINT",EDGE,{"disambiguationData":[TD([[subQ2,-1.0]])],"derivedFrom":subQ1}),1.0]])]});}
            var Q86;
            {var subQ0=sQuery(id+"F0.wireOp",EDGE,"E22");var subQ1=sQuery(id+"F0.wireOp",EDGE,"E13.bottom");var subQ2=makeQuery(id+"F0.imprint","INTERSECT",VERTEX,{"derivedFrom":[subQ1,subQ0]});Q86=makeQuery(id+"F0.imprint","IMPRINT",FACE,{"disambiguationData":[TD([[makeQuery(id+"F0.imprint","IMPRINT",EDGE,{"disambiguationData":[TD([[subQ2,-1.0]])],"derivedFrom":subQ1}),-1.0]])]});}
            var Q87;
            {var subQ1=sQuery(id+"F0.wireOp",EDGE,"E13.bottom");var subQ3=sQuery(id+"F0.wireOp",EDGE,"E40");var subQ4=makeQuery(id+"F0.imprint","INTERSECT",VERTEX,{"disambiguationData":[OD(1.0)],"derivedFrom":[subQ1,subQ3]});Q87=makeQuery(id+"F0.imprint","IMPRINT",FACE,{"disambiguationData":[TD([[makeQuery(id+"F0.imprint","IMPRINT",EDGE,{"disambiguationData":[TD([[subQ4,-1.0]])],"derivedFrom":subQ1}),-1.0]])]});}
            var Q88;
            {var subQ1=sQuery(id+"F0.wireOp",EDGE,"E13.bottom");var subQ3=sQuery(id+"F0.wireOp",EDGE,"E40");var subQ4=makeQuery(id+"F0.imprint","INTERSECT",VERTEX,{"disambiguationData":[OD(0.0)],"derivedFrom":[subQ1,subQ3]});Q88=makeQuery(id+"F0.imprint","IMPRINT",FACE,{"disambiguationData":[TD([[makeQuery(id+"F0.imprint","IMPRINT",EDGE,{"disambiguationData":[TD([[subQ4,1.0]])],"derivedFrom":subQ1}),-1.0]])]});}
            var Q89;
            {var subQ0=sQuery(id+"F0.wireOp",EDGE,"E40");var subQ1=sQuery(id+"F0.wireOp",EDGE,"E13.bottom");var subQ2=makeQuery(id+"F0.imprint","INTERSECT",VERTEX,{"disambiguationData":[OD(0.0)],"derivedFrom":[subQ1,subQ0]});Q89=makeQuery(id+"F0.imprint","IMPRINT",FACE,{"disambiguationData":[TD([[makeQuery(id+"F0.imprint","IMPRINT",EDGE,{"disambiguationData":[TD([[subQ2,-1.0]])],"derivedFrom":subQ1}),-1.0]])]});}
            var Q90;
            {var subQ0=sQuery(id+"F0.wireOp",EDGE,"E77");Q90=makeQuery(id+"F0.imprint","IMPRINT",FACE,{"disambiguationData":[TD([[makeQuery(id+"F0.imprint","IMPRINT",EDGE,{"derivedFrom":subQ0}),-1.0]])]});}
            var Q91;
            {var subQ0=sQuery(id+"F0.wireOp",EDGE,"E82.MirrorCS");Q91=makeQuery(id+"F0.imprint","IMPRINT",FACE,{"disambiguationData":[TD([[makeQuery(id+"F0.imprint","IMPRINT",EDGE,{"derivedFrom":subQ0}),1.0]])]});}
            var Q92;
            {var subQ5=sQuery(id+"F0.wireOp",EDGE,"E61");var subQ6=sQuery(id+"F0.wireOp",EDGE,"E15.left");var subQ7=makeQuery(id+"F0.imprint","INTERSECT",VERTEX,{"derivedFrom":[subQ6,subQ5]});Q92=makeQuery(id+"F0.imprint","IMPRINT",FACE,{"disambiguationData":[TD([[makeQuery(id+"F0.imprint","IMPRINT",EDGE,{"disambiguationData":[TD([[subQ7,1.0]])],"derivedFrom":subQ6}),1.0]])]});}
            var Q93;
            {var subQ0=sQuery(id+"F0.wireOp",EDGE,"E91");var subQ1=sQuery(id+"F0.wireOp",EDGE,"E13.top");var subQ2=makeQuery(id+"F0.imprint","INTERSECT",VERTEX,{"derivedFrom":[subQ1,subQ0]});Q93=makeQuery(id+"F0.imprint","IMPRINT",FACE,{"disambiguationData":[TD([[makeQuery(id+"F0.imprint","IMPRINT",EDGE,{"disambiguationData":[TD([[subQ2,-1.0]])],"derivedFrom":subQ1}),-1.0]])]});}
            var Q94;
            {var subQ0=sQuery(id+"F0.wireOp",EDGE,"E90");var subQ1=sQuery(id+"F0.wireOp",EDGE,"E10.bottom");var subQ2=makeQuery(id+"F0.imprint","INTERSECT",VERTEX,{"derivedFrom":[subQ1,subQ0]});Q94=makeQuery(id+"F0.imprint","IMPRINT",FACE,{"disambiguationData":[TD([[makeQuery(id+"F0.imprint","IMPRINT",EDGE,{"disambiguationData":[TD([[subQ2,-1.0]])],"derivedFrom":subQ1}),1.0]])]});}
            var Q95;
            {var subQ0=sQuery(id+"F0.wireOp",EDGE,"E84");var subQ1=sQuery(id+"F0.wireOp",EDGE,"E2.left");var subQ2=makeQuery(id+"F0.imprint","INTERSECT",VERTEX,{"derivedFrom":[subQ1,subQ0]});Q95=makeQuery(id+"F0.imprint","IMPRINT",FACE,{"disambiguationData":[TD([[makeQuery(id+"F0.imprint","IMPRINT",EDGE,{"disambiguationData":[TD([[subQ2,-1.0]])],"derivedFrom":subQ1}),-1.0]])]});}
            var Q96;
            {var subQ0=sQuery(id+"F0.wireOp",EDGE,"E86");var subQ1=sQuery(id+"F0.wireOp",EDGE,"E13.top");var subQ2=makeQuery(id+"F0.imprint","INTERSECT",VERTEX,{"derivedFrom":[subQ1,subQ0]});Q96=makeQuery(id+"F0.imprint","IMPRINT",FACE,{"disambiguationData":[TD([[makeQuery(id+"F0.imprint","IMPRINT",EDGE,{"disambiguationData":[TD([[subQ2,1.0]])],"derivedFrom":subQ1}),-1.0]])]});}
            var Q97;
            {var subQ5=sQuery(id+"F0.wireOp",EDGE,"E10.bottom");var subQ7=sQuery(id+"F0.wireOp",EDGE,"E85");var subQ8=makeQuery(id+"F0.imprint","INTERSECT",VERTEX,{"derivedFrom":[subQ5,subQ7]});Q97=makeQuery(id+"F0.imprint","IMPRINT",FACE,{"disambiguationData":[TD([[makeQuery(id+"F0.imprint","IMPRINT",EDGE,{"disambiguationData":[TD([[subQ8,1.0]])],"derivedFrom":subQ5}),1.0]])]});}
            var Q98;
            {var subQ0=sQuery(id+"F0.wireOp",EDGE,"E86");var subQ1=sQuery(id+"F0.wireOp",EDGE,"E2.left");var subQ2=makeQuery(id+"F0.imprint","INTERSECT",VERTEX,{"derivedFrom":[subQ1,subQ0]});Q98=makeQuery(id+"F0.imprint","IMPRINT",FACE,{"disambiguationData":[TD([[makeQuery(id+"F0.imprint","IMPRINT",EDGE,{"disambiguationData":[TD([[subQ2,-1.0]])],"derivedFrom":subQ1}),-1.0]])]});}
            var Q99;
            {var subQ0=sQuery(id+"F0.wireOp",EDGE,"E86");var subQ1=sQuery(id+"F0.wireOp",EDGE,"E84");var subQ2=makeQuery(id+"F0.imprint","INTERSECT",VERTEX,{"derivedFrom":[subQ1,subQ0]});Q99=makeQuery(id+"F0.imprint","IMPRINT",FACE,{"disambiguationData":[TD([[makeQuery(id+"F0.imprint","IMPRINT",EDGE,{"disambiguationData":[TD([[subQ2,-1.0]])],"derivedFrom":subQ1}),1.0]])]});}
            var Q100;
            {var subQ0=sQuery(id+"F0.wireOp",EDGE,"E53");Q100=makeQuery(id+"F0.imprint","IMPRINT",FACE,{"disambiguationData":[TD([[makeQuery(id+"F0.imprint","IMPRINT",EDGE,{"derivedFrom":subQ0}),1.0]])]});}
            var Q101;
            {var subQ1=sQuery(id+"F0.wireOp",EDGE,"E57");var subQ3=sQuery(id+"F0.wireOp",EDGE,"E90");var subQ4=makeQuery(id+"F0.imprint","INTERSECT",VERTEX,{"derivedFrom":[subQ1,subQ3]});Q101=makeQuery(id+"F0.imprint","IMPRINT",FACE,{"disambiguationData":[TD([[makeQuery(id+"F0.imprint","IMPRINT",EDGE,{"disambiguationData":[TD([[subQ4,1.0]])],"derivedFrom":subQ3}),1.0]])]});}
            var Q102;
            {var subQ1=sQuery(id+"F0.wireOp",EDGE,"E61");var subQ3=sQuery(id+"F0.wireOp",EDGE,"E90");var subQ4=makeQuery(id+"F0.imprint","INTERSECT",VERTEX,{"derivedFrom":[subQ1,subQ3]});Q102=makeQuery(id+"F0.imprint","IMPRINT",FACE,{"disambiguationData":[TD([[makeQuery(id+"F0.imprint","IMPRINT",EDGE,{"disambiguationData":[TD([[subQ4,1.0]])],"derivedFrom":subQ3}),-1.0]])]});}
            var Q103;
            {var subQ1=sQuery(id+"F0.wireOp",EDGE,"E62");var subQ3=sQuery(id+"F0.wireOp",EDGE,"E91");var subQ4=makeQuery(id+"F0.imprint","INTERSECT",VERTEX,{"derivedFrom":[subQ1,subQ3]});Q103=makeQuery(id+"F0.imprint","IMPRINT",FACE,{"disambiguationData":[TD([[makeQuery(id+"F0.imprint","IMPRINT",EDGE,{"disambiguationData":[TD([[subQ4,1.0]])],"derivedFrom":subQ3}),1.0]])]});}
            var Q104;
            {var subQ1=sQuery(id+"F0.wireOp",EDGE,"E55");var subQ3=sQuery(id+"F0.wireOp",EDGE,"E91");var subQ4=makeQuery(id+"F0.imprint","INTERSECT",VERTEX,{"derivedFrom":[subQ1,subQ3]});Q104=makeQuery(id+"F0.imprint","IMPRINT",FACE,{"disambiguationData":[TD([[makeQuery(id+"F0.imprint","IMPRINT",EDGE,{"disambiguationData":[TD([[subQ4,1.0]])],"derivedFrom":subQ3}),-1.0]])]});}
            var Q105;
            {var subQ5=sQuery(id+"F0.wireOp",EDGE,"E87");var subQ6=sQuery(id+"F0.wireOp",EDGE,"E84");var subQ7=makeQuery(id+"F0.imprint","INTERSECT",VERTEX,{"derivedFrom":[subQ6,subQ5]});Q105=makeQuery(id+"F0.imprint","IMPRINT",FACE,{"disambiguationData":[TD([[makeQuery(id+"F0.imprint","IMPRINT",EDGE,{"disambiguationData":[TD([[subQ7,-1.0]])],"derivedFrom":subQ6}),-1.0]])]});}
            var Q106;
            {var subQ5=sQuery(id+"F0.wireOp",EDGE,"E94");var subQ7=sQuery(id+"F0.wireOp",EDGE,"E2.left");var subQ8=makeQuery(id+"F0.imprint","INTERSECT",VERTEX,{"derivedFrom":[subQ7,subQ5]});Q106=makeQuery(id+"F0.imprint","IMPRINT",FACE,{"disambiguationData":[TD([[makeQuery(id+"F0.imprint","IMPRINT",EDGE,{"disambiguationData":[TD([[subQ8,-1.0]])],"derivedFrom":subQ7}),-1.0]])]});}
            var Q107;
            {var subQ3=sQuery(id+"F0.wireOp",EDGE,"E2.left");var subQ6=sQuery(id+"F0.wireOp",EDGE,"E94");var subQ8=makeQuery(id+"F0.imprint","INTERSECT",VERTEX,{"derivedFrom":[subQ3,subQ6]});Q107=makeQuery(id+"F0.imprint","IMPRINT",FACE,{"disambiguationData":[TD([[makeQuery(id+"F0.imprint","IMPRINT",EDGE,{"disambiguationData":[TD([[subQ8,-1.0]])],"derivedFrom":subQ3}),1.0]])]});}
            var Q108;
            {var subQ0=sQuery(id+"F0.wireOp",EDGE,"E102.MirrorCS");var subQ1=sQuery(id+"F0.wireOp",EDGE,"E2.right");var subQ2=makeQuery(id+"F0.imprint","INTERSECT",VERTEX,{"derivedFrom":[subQ1,subQ0]});Q108=makeQuery(id+"F0.imprint","IMPRINT",FACE,{"disambiguationData":[TD([[makeQuery(id+"F0.imprint","IMPRINT",EDGE,{"disambiguationData":[TD([[subQ2,-1.0]])],"derivedFrom":subQ1}),1.0]])]});}
            var Q109;
            {var subQ5=sQuery(id+"F0.wireOp",EDGE,"E102.MirrorCS");var subQ6=sQuery(id+"F0.wireOp",EDGE,"E96.MirrorCS");var subQ7=makeQuery(id+"F0.imprint","INTERSECT",VERTEX,{"derivedFrom":[subQ6,subQ5]});Q109=makeQuery(id+"F0.imprint","IMPRINT",FACE,{"disambiguationData":[TD([[makeQuery(id+"F0.imprint","IMPRINT",EDGE,{"disambiguationData":[TD([[subQ7,-1.0]])],"derivedFrom":subQ6}),1.0]])]});}
            var Q110;
            {var subQ3=sQuery(id+"F0.wireOp",EDGE,"E99.MirrorCS");var subQ8=sQuery(id+"F0.wireOp",EDGE,"E13.top");var subQ11=makeQuery(id+"F0.imprint","INTERSECT",VERTEX,{"derivedFrom":[subQ8,subQ3]});Q110=makeQuery(id+"F0.imprint","IMPRINT",FACE,{"disambiguationData":[TD([[makeQuery(id+"F0.imprint","IMPRINT",EDGE,{"disambiguationData":[TD([[subQ11,1.0]])],"derivedFrom":subQ8}),-1.0]])]});}
            var Q111;
            {var subQ5=sQuery(id+"F0.wireOp",EDGE,"E10.bottom");var subQ9=sQuery(id+"F0.wireOp",EDGE,"E101.MirrorCS");var subQ11=makeQuery(id+"F0.imprint","INTERSECT",VERTEX,{"derivedFrom":[subQ5,subQ9]});Q111=makeQuery(id+"F0.imprint","IMPRINT",FACE,{"disambiguationData":[TD([[makeQuery(id+"F0.imprint","IMPRINT",EDGE,{"disambiguationData":[TD([[subQ11,1.0]])],"derivedFrom":subQ5}),1.0]])]});}
            var Q112;
            {var subQ7=sQuery(id+"F0.wireOp",EDGE,"E69.MirrorCS");Q112=makeQuery(id+"F0.imprint","IMPRINT",FACE,{"disambiguationData":[TD([[makeQuery(id+"F0.imprint","IMPRINT",EDGE,{"derivedFrom":subQ7}),-1.0]])]});}
            var Q113;
            {var subQ1=sQuery(id+"F0.wireOp",EDGE,"E14.left");var subQ7=sQuery(id+"F0.wireOp",EDGE,"E65.MirrorCS");var subQ9=makeQuery(id+"F0.imprint","INTERSECT",VERTEX,{"derivedFrom":[subQ1,subQ7]});Q113=makeQuery(id+"F0.imprint","IMPRINT",FACE,{"disambiguationData":[TD([[makeQuery(id+"F0.imprint","IMPRINT",EDGE,{"disambiguationData":[TD([[subQ9,-1.0]])],"derivedFrom":subQ1}),-1.0]])]});}
            var Q114;
            {var subQ1=sQuery(id+"F0.wireOp",EDGE,"E65.MirrorCS");var subQ3=sQuery(id+"F0.wireOp",EDGE,"E99.MirrorCS");var subQ4=makeQuery(id+"F0.imprint","INTERSECT",VERTEX,{"derivedFrom":[subQ1,subQ3]});Q114=makeQuery(id+"F0.imprint","IMPRINT",FACE,{"disambiguationData":[TD([[makeQuery(id+"F0.imprint","IMPRINT",EDGE,{"disambiguationData":[TD([[subQ4,1.0]])],"derivedFrom":subQ3}),-1.0]])]});}
            var Q115;
            {var subQ1=sQuery(id+"F0.wireOp",EDGE,"E64.MirrorCS");var subQ3=sQuery(id+"F0.wireOp",EDGE,"E99.MirrorCS");var subQ4=makeQuery(id+"F0.imprint","INTERSECT",VERTEX,{"derivedFrom":[subQ1,subQ3]});Q115=makeQuery(id+"F0.imprint","IMPRINT",FACE,{"disambiguationData":[TD([[makeQuery(id+"F0.imprint","IMPRINT",EDGE,{"disambiguationData":[TD([[subQ4,1.0]])],"derivedFrom":subQ3}),1.0]])]});}
            var Q116;
            {var subQ0=sQuery(id+"F0.wireOp",EDGE,"E100.MirrorCS");var subQ1=sQuery(id+"F0.wireOp",EDGE,"E98.MirrorCS");var subQ2=makeQuery(id+"F0.imprint","INTERSECT",VERTEX,{"derivedFrom":[subQ1,subQ0]});Q116=makeQuery(id+"F0.imprint","IMPRINT",FACE,{"disambiguationData":[TD([[makeQuery(id+"F0.imprint","IMPRINT",EDGE,{"disambiguationData":[TD([[subQ2,-1.0]])],"derivedFrom":subQ1}),-1.0]])]});}
            var Q117;
            {var subQ1=sQuery(id+"F0.wireOp",EDGE,"E98.MirrorCS");var subQ3=sQuery(id+"F0.wireOp",EDGE,"E100.MirrorCS");var subQ4=makeQuery(id+"F0.imprint","INTERSECT",VERTEX,{"derivedFrom":[subQ1,subQ3]});Q117=makeQuery(id+"F0.imprint","IMPRINT",FACE,{"disambiguationData":[TD([[makeQuery(id+"F0.imprint","IMPRINT",EDGE,{"disambiguationData":[TD([[subQ4,-1.0]])],"derivedFrom":subQ3}),1.0]])]});}
            var Q118;
            {var subQ1=sQuery(id+"F0.wireOp",EDGE,"E66.MirrorCS");var subQ3=sQuery(id+"F0.wireOp",EDGE,"E101.MirrorCS");var subQ4=makeQuery(id+"F0.imprint","INTERSECT",VERTEX,{"derivedFrom":[subQ1,subQ3]});Q118=makeQuery(id+"F0.imprint","IMPRINT",FACE,{"disambiguationData":[TD([[makeQuery(id+"F0.imprint","IMPRINT",EDGE,{"disambiguationData":[TD([[subQ4,1.0]])],"derivedFrom":subQ3}),1.0]])]});}
            var Q119;
            {var subQ0=sQuery(id+"F0.wireOp",EDGE,"E67.MirrorCS");Q119=makeQuery(id+"F0.imprint","IMPRINT",FACE,{"disambiguationData":[TD([[makeQuery(id+"F0.imprint","IMPRINT",EDGE,{"derivedFrom":subQ0}),-1.0]])]});}
            var Q120;
            {var subQ5=sQuery(id+"F0.wireOp",EDGE,"E104.MirrorCS");var subQ9=sQuery(id+"F0.wireOp",EDGE,"E13.top");var subQ11=makeQuery(id+"F0.imprint","INTERSECT",VERTEX,{"derivedFrom":[subQ9,subQ5]});Q120=makeQuery(id+"F0.imprint","IMPRINT",FACE,{"disambiguationData":[TD([[makeQuery(id+"F0.imprint","IMPRINT",EDGE,{"disambiguationData":[TD([[subQ11,-1.0]])],"derivedFrom":subQ9}),-1.0]])]});}
            var Q121;
            {var subQ1=sQuery(id+"F0.wireOp",EDGE,"E2.right");var subQ7=sQuery(id+"F0.wireOp",EDGE,"E96.MirrorCS");var subQ8=makeQuery(id+"F0.imprint","INTERSECT",VERTEX,{"derivedFrom":[subQ1,subQ7]});Q121=makeQuery(id+"F0.imprint","IMPRINT",FACE,{"disambiguationData":[TD([[makeQuery(id+"F0.imprint","IMPRINT",EDGE,{"disambiguationData":[TD([[subQ8,-1.0]])],"derivedFrom":subQ1}),1.0]])]});}
            var Q122;
            {var subQ3=sQuery(id+"F0.wireOp",EDGE,"E105.MirrorCS");var subQ9=sQuery(id+"F0.wireOp",EDGE,"E96.MirrorCS");var subQ11=makeQuery(id+"F0.imprint","INTERSECT",VERTEX,{"derivedFrom":[subQ9,subQ3]});Q122=makeQuery(id+"F0.imprint","IMPRINT",FACE,{"disambiguationData":[TD([[makeQuery(id+"F0.imprint","IMPRINT",EDGE,{"disambiguationData":[TD([[subQ11,-1.0]])],"derivedFrom":subQ9}),1.0]])]});}
            var Q123;
            {var subQ0=sQuery(id+"F0.wireOp",EDGE,"E97.MirrorCS");var subQ1=sQuery(id+"F0.wireOp",EDGE,"E10.bottom");var subQ2=makeQuery(id+"F0.imprint","INTERSECT",VERTEX,{"derivedFrom":[subQ1,subQ0]});Q123=makeQuery(id+"F0.imprint","IMPRINT",FACE,{"disambiguationData":[TD([[makeQuery(id+"F0.imprint","IMPRINT",EDGE,{"disambiguationData":[TD([[subQ2,-1.0]])],"derivedFrom":subQ1}),1.0]])]});}
            var Q124;
            {var subQ0=sQuery(id+"F0.wireOp",EDGE,"E104.MirrorCS");var subQ1=sQuery(id+"F0.wireOp",EDGE,"E2.right");var subQ2=makeQuery(id+"F0.imprint","INTERSECT",VERTEX,{"derivedFrom":[subQ1,subQ0]});Q124=makeQuery(id+"F0.imprint","IMPRINT",FACE,{"disambiguationData":[TD([[makeQuery(id+"F0.imprint","IMPRINT",EDGE,{"disambiguationData":[TD([[subQ2,-1.0]])],"derivedFrom":subQ1}),1.0]])]});}
            var Q125;
            {var subQ4=sQuery(id+"F0.wireOp",EDGE,"E2.left");var subQ5=makeQuery(id+"F0.imprint","INTERSECT",VERTEX,{"derivedFrom":[subQ4,sQuery(id+"F0.wireOp",EDGE,"E86")]});Q125=makeQuery(id+"F0.imprint","IMPRINT",FACE,{"disambiguationData":[TD([[makeQuery(id+"F0.imprint","IMPRINT",EDGE,{"disambiguationData":[TD([[subQ5,1.0]])],"derivedFrom":subQ4}),1.0]])]});}
            var Q126;
            {var subQ3=sQuery(id+"F0.wireOp",EDGE,"E94");var subQ6=sQuery(id+"F0.wireOp",EDGE,"E84");var subQ11=makeQuery(id+"F0.imprint","INTERSECT",VERTEX,{"derivedFrom":[subQ6,subQ3]});Q126=makeQuery(id+"F0.imprint","IMPRINT",FACE,{"disambiguationData":[TD([[makeQuery(id+"F0.imprint","IMPRINT",EDGE,{"disambiguationData":[TD([[subQ11,-1.0]])],"derivedFrom":subQ6}),1.0]])]});}
            var Q127;
            {var subQ0=sQuery(id+"F0.wireOp",EDGE,"E102.MirrorCS");var subQ1=sQuery(id+"F0.wireOp",EDGE,"E96.MirrorCS");var subQ2=makeQuery(id+"F0.imprint","INTERSECT",VERTEX,{"derivedFrom":[subQ1,subQ0]});Q127=makeQuery(id+"F0.imprint","IMPRINT",FACE,{"disambiguationData":[TD([[makeQuery(id+"F0.imprint","IMPRINT",EDGE,{"disambiguationData":[TD([[subQ2,-1.0]])],"derivedFrom":subQ1}),-1.0]])]});}
            var Q128;
            {var subQ0=sQuery(id+"F0.wireOp",EDGE,"E93");var subQ1=sQuery(id+"F0.wireOp",EDGE,"E92");var subQ2=makeQuery(id+"F0.imprint","INTERSECT",VERTEX,{"derivedFrom":[subQ1,subQ0]});Q128=makeQuery(id+"F0.imprint","IMPRINT",FACE,{"disambiguationData":[TD([[makeQuery(id+"F0.imprint","IMPRINT",EDGE,{"disambiguationData":[TD([[subQ2,-1.0]])],"derivedFrom":subQ1}),1.0]])]});}
            var Q129;
            {var subQ1=sQuery(id+"F0.wireOp",EDGE,"E92");var subQ3=sQuery(id+"F0.wireOp",EDGE,"E93");var subQ4=makeQuery(id+"F0.imprint","INTERSECT",VERTEX,{"derivedFrom":[subQ1,subQ3]});Q129=makeQuery(id+"F0.imprint","IMPRINT",FACE,{"disambiguationData":[TD([[makeQuery(id+"F0.imprint","IMPRINT",EDGE,{"disambiguationData":[TD([[subQ4,-1.0]])],"derivedFrom":subQ3}),-1.0]])]});}
            var Q130;
            {var subQ0=sQuery(id+"F0.wireOp",EDGE,"E94");var subQ1=sQuery(id+"F0.wireOp",EDGE,"E84");var subQ2=makeQuery(id+"F0.imprint","INTERSECT",VERTEX,{"derivedFrom":[subQ1,subQ0]});Q130=makeQuery(id+"F0.imprint","IMPRINT",FACE,{"disambiguationData":[TD([[makeQuery(id+"F0.imprint","IMPRINT",EDGE,{"disambiguationData":[TD([[subQ2,-1.0]])],"derivedFrom":subQ1}),-1.0]])]});}
            var Q131;
            {var subQ0=sQuery(id+"F0.wireOp",EDGE,"E87");var subQ1=sQuery(id+"F0.wireOp",EDGE,"E84");var subQ2=makeQuery(id+"F0.imprint","INTERSECT",VERTEX,{"derivedFrom":[subQ1,subQ0]});Q131=makeQuery(id+"F0.imprint","IMPRINT",FACE,{"disambiguationData":[TD([[makeQuery(id+"F0.imprint","IMPRINT",EDGE,{"disambiguationData":[TD([[subQ2,-1.0]])],"derivedFrom":subQ1}),1.0]])]});}
            var Q132;
            {var subQ0=sQuery(id+"F0.wireOp",EDGE,"E95");var subQ1=sQuery(id+"F0.wireOp",EDGE,"E85");var subQ2=makeQuery(id+"F0.imprint","INTERSECT",VERTEX,{"derivedFrom":[subQ1,subQ0]});Q132=makeQuery(id+"F0.imprint","IMPRINT",FACE,{"disambiguationData":[TD([[makeQuery(id+"F0.imprint","IMPRINT",EDGE,{"disambiguationData":[TD([[subQ2,-1.0]])],"derivedFrom":subQ1}),-1.0]])]});}
            var Q133;
            {var subQ0=sQuery(id+"F0.wireOp",EDGE,"E86");var subQ1=sQuery(id+"F0.wireOp",EDGE,"E85");var subQ2=makeQuery(id+"F0.imprint","INTERSECT",VERTEX,{"derivedFrom":[subQ1,subQ0]});Q133=makeQuery(id+"F0.imprint","IMPRINT",FACE,{"disambiguationData":[TD([[makeQuery(id+"F0.imprint","IMPRINT",EDGE,{"disambiguationData":[TD([[subQ2,-1.0]])],"derivedFrom":subQ1}),1.0]])]});}
            var Q134;
            {var subQ0=sQuery(id+"F0.wireOp",EDGE,"E94");var subQ1=sQuery(id+"F0.wireOp",EDGE,"E85");var subQ2=makeQuery(id+"F0.imprint","INTERSECT",VERTEX,{"derivedFrom":[subQ1,subQ0]});Q134=makeQuery(id+"F0.imprint","IMPRINT",FACE,{"disambiguationData":[TD([[makeQuery(id+"F0.imprint","IMPRINT",EDGE,{"disambiguationData":[TD([[subQ2,-1.0]])],"derivedFrom":subQ1}),-1.0]])]});}
            var Q135;
            {var subQ0=sQuery(id+"F0.wireOp",EDGE,"E104.MirrorCS");var subQ1=sQuery(id+"F0.wireOp",EDGE,"E96.MirrorCS");var subQ2=makeQuery(id+"F0.imprint","INTERSECT",VERTEX,{"derivedFrom":[subQ1,subQ0]});Q135=makeQuery(id+"F0.imprint","IMPRINT",FACE,{"disambiguationData":[TD([[makeQuery(id+"F0.imprint","IMPRINT",EDGE,{"disambiguationData":[TD([[subQ2,-1.0]])],"derivedFrom":subQ1}),-1.0]])]});}
            var Q136;
            {var subQ0=sQuery(id+"F0.wireOp",EDGE,"E102.MirrorCS");var subQ1=sQuery(id+"F0.wireOp",EDGE,"E97.MirrorCS");var subQ2=makeQuery(id+"F0.imprint","INTERSECT",VERTEX,{"derivedFrom":[subQ1,subQ0]});Q136=makeQuery(id+"F0.imprint","IMPRINT",FACE,{"disambiguationData":[TD([[makeQuery(id+"F0.imprint","IMPRINT",EDGE,{"disambiguationData":[TD([[subQ2,-1.0]])],"derivedFrom":subQ1}),1.0]])]});}
            var Q137;
            {var subQ0=sQuery(id+"F0.wireOp",EDGE,"E104.MirrorCS");var subQ1=sQuery(id+"F0.wireOp",EDGE,"E97.MirrorCS");var subQ2=makeQuery(id+"F0.imprint","INTERSECT",VERTEX,{"derivedFrom":[subQ1,subQ0]});Q137=makeQuery(id+"F0.imprint","IMPRINT",FACE,{"disambiguationData":[TD([[makeQuery(id+"F0.imprint","IMPRINT",EDGE,{"disambiguationData":[TD([[subQ2,-1.0]])],"derivedFrom":subQ1}),-1.0]])]});}
            var Q138;
            {var subQ0=sQuery(id+"F0.wireOp",EDGE,"E103.MirrorCS");var subQ1=sQuery(id+"F0.wireOp",EDGE,"E97.MirrorCS");var subQ2=makeQuery(id+"F0.imprint","INTERSECT",VERTEX,{"derivedFrom":[subQ1,subQ0]});Q138=makeQuery(id+"F0.imprint","IMPRINT",FACE,{"disambiguationData":[TD([[makeQuery(id+"F0.imprint","IMPRINT",EDGE,{"disambiguationData":[TD([[subQ2,-1.0]])],"derivedFrom":subQ1}),1.0]])]});}
            var Q139;
            {var subQ0=sQuery(id+"F0.wireOp",EDGE,"E105.MirrorCS");var subQ1=sQuery(id+"F0.wireOp",EDGE,"E96.MirrorCS");var subQ2=makeQuery(id+"F0.imprint","INTERSECT",VERTEX,{"derivedFrom":[subQ1,subQ0]});Q139=makeQuery(id+"F0.imprint","IMPRINT",FACE,{"disambiguationData":[TD([[makeQuery(id+"F0.imprint","IMPRINT",EDGE,{"disambiguationData":[TD([[subQ2,-1.0]])],"derivedFrom":subQ1}),-1.0]])]});}
            extrude(context, id + "F1", {"entities" : qUnion([Q0, Q1, Q2, Q3, Q4, Q5, Q6, Q7, Q8, Q9, Q10, Q11, Q12, Q13, Q14, Q15, Q16, Q17, Q18, Q19, Q20, Q21, Q22, Q23, Q24, Q25, Q26, Q27, Q28, Q29, Q30, Q31, Q32, Q33, Q34, Q35, Q36, Q37, Q38, Q39, Q40, Q41, Q42, Q43, Q44, Q45, Q46, Q47, Q48, Q49, Q50, Q51, Q52, Q53, Q54, Q55, Q56, Q57, Q58, Q59, Q60, Q61, Q62, Q63, Q64, Q65, Q66, Q67, Q68, Q69, Q70, Q71, Q72, Q73, Q74, Q75, Q76, Q77, Q78, Q79, Q80, Q81, Q82, Q83, Q84, Q85, Q86, Q87, Q88, Q89, Q90, Q91, Q92, Q93, Q94, Q95, Q96, Q97, Q98, Q99, Q100, Q101, Q102, Q103, Q104, Q105, Q106, Q107, Q108, Q109, Q110, Q111, Q112, Q113, Q114, Q115, Q116, Q117, Q118, Q119, Q120, Q121, Q122, Q123, Q124, Q125, Q126, Q127, Q128, Q129, Q130, Q131, Q132, Q133, Q134, Q135, Q136, Q137, Q138, Q139]), "depth" : 5 * mm});
        }
        {
            var Q0;
            Q0=makeQuery(id+"F0.imprint","IMPRINT",FACE,{"disambiguationData":[TD([[makeQuery(id+"F0.imprint","IMPRINT",EDGE,{"derivedFrom":sQuery(id+"F0.wireOp",EDGE,"E8")}),-1.0]])]});
            var Q1;
            {var subQ0=sQuery(id+"F0.wireOp",EDGE,"E40");var subQ1=sQuery(id+"F0.wireOp",EDGE,"E9");var subQ2=makeQuery(id+"F0.imprint","INTERSECT",VERTEX,{"disambiguationData":[OD(0.0)],"derivedFrom":[subQ1,subQ0]});Q1=makeQuery(id+"F0.imprint","IMPRINT",FACE,{"disambiguationData":[TD([[makeQuery(id+"F0.imprint","IMPRINT",EDGE,{"disambiguationData":[TD([[subQ2,-1.0]])],"derivedFrom":subQ1}),1.0]])]});}
            var Q2;
            {var subQ0=sQuery(id+"F0.wireOp",EDGE,"E41.bottom");var subQ1=sQuery(id+"F0.wireOp",EDGE,"E9");var subQ2=makeQuery(id+"F0.imprint","INTERSECT",VERTEX,{"disambiguationData":[OD(0.0)],"derivedFrom":[subQ1,subQ0]});Q2=makeQuery(id+"F0.imprint","IMPRINT",FACE,{"disambiguationData":[TD([[makeQuery(id+"F0.imprint","IMPRINT",EDGE,{"disambiguationData":[TD([[subQ2,-1.0]])],"derivedFrom":subQ1}),1.0]])]});}
            extrude(context, id + "F2", {"entities" : qUnion([Q0, Q1, Q2]), "operationType" : NewBodyOperationType.ADD, "depth" : 8 * mm});
        }
        {
            var Q0;
            Q0=makeQuery(id+"F2.opExtrude","CAP_EDGE",EDGE,{"disambiguationData":[OSD([sQuery(id+"F0.wireOp",EDGE,"E9")])],"isStart":false});
            fillet(context, id + "F3", {"entities" : qUnion([Q0]), "radius" : 0.4 * mm, "tangentPropagation" : true, "allowEdgeOverflow" : false});
        }
    });
